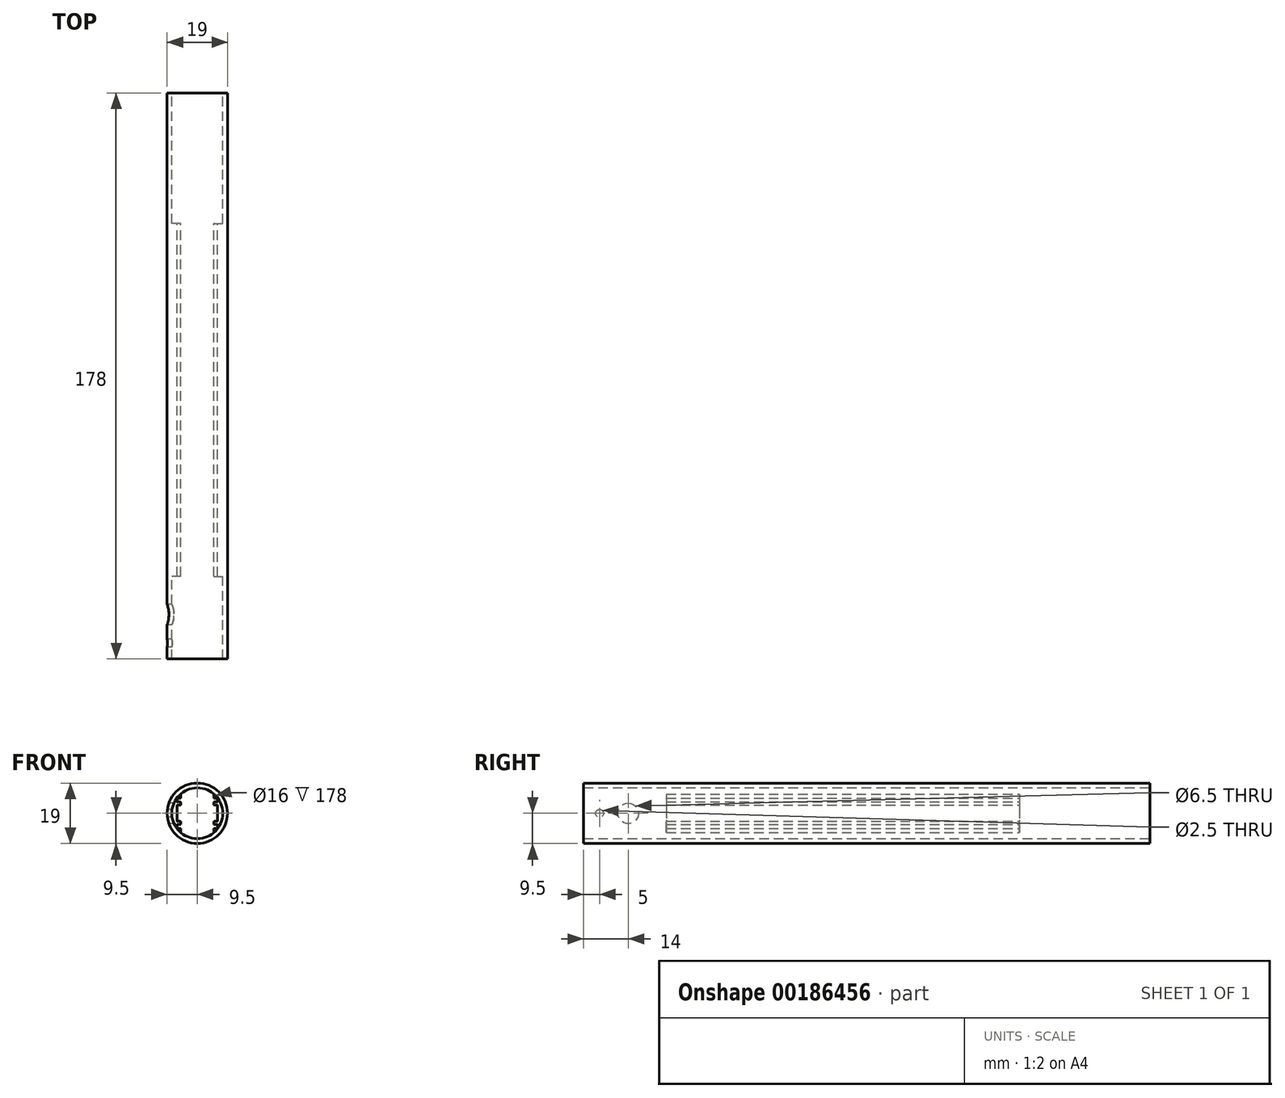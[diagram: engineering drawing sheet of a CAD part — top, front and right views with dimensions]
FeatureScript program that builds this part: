
annotation { "Feature Type Name" : "Feature", "Feature Type Description" : "" }
export const myFeature = defineFeature(function(context is Context, id is Id, definition is map)
    precondition{}
    {
        {
            assignVariable(context, id + "F0", {"name" : "Main_Diam", "anyValue" : 19});
        }
        {
            assignVariable(context, id + "F1", {"name" : "Main_Length", "anyValue" : 178});
        }
        {
            assignVariable(context, id + "F2", {"name" : "Bore_Depth_F", "anyValue" : 26});
        }
        {
            assignVariable(context, id + "F3", {"name" : "Bore_Depth_R", "anyValue" : 41});
        }
        {
            var Q0;
            Q0=qCreatedBy(makeId("Front.planeOp"),FACE);
            var sketch = newSketch(context, id + "F4", { "sketchPlane" : qUnion([Q0])});
            skLineSegment(sketch, "E0", {"start": v(-5.25, -3.45) * mm, "end": v(-5.25, -2.65) * mm});
            skLineSegment(sketch, "E1", {"start": v(9.2, 1.38) * mm, "end": v(9.42, 1.2) * mm});
            skArc(sketch, "E2", {"start": v(-5.35, -2.55) * mm, "mid": v(-5.28, -2.58) * mm, "end": v(-5.25, -2.65) * mm});
            skArc(sketch, "E3", {"start": v(6.3, 4.75) * mm, "mid": v(6.37, 4.72) * mm, "end": v(6.4, 4.65) * mm});
            skArc(sketch, "E4", {"start": v(-5.25, -6.04) * mm, "mid": v(0, -8) * mm, "end": v(5.25, -6.04) * mm});
            skLineSegment(sketch, "E5", {"start": v(1.53, 9.17) * mm, "end": v(1.78, 9.33) * mm});
            skLineSegment(sketch, "E6", {"start": v(-7.18, -5.91) * mm, "end": v(-7.2, -6.2) * mm});
            skArc(sketch, "E7", {"start": v(-8.33, -4.58) * mm, "mid": v(-8.23, -4.75) * mm, "end": v(-8.13, -4.92) * mm});
            skLineSegment(sketch, "E8", {"start": v(5.13, 7.76) * mm, "end": v(5.42, 7.8) * mm});
            skLineSegment(sketch, "E9", {"start": v(6.4, -2.45) * mm, "end": v(6.4, 0) * mm});
            skLineSegment(sketch, "E10", {"start": v(-2.33, -9) * mm, "end": v(-2.17, -9.25) * mm});
            skArc(sketch, "E11", {"start": v(8.97, -3.13) * mm, "mid": v(9.04, -2.94) * mm, "end": v(9.1, -2.74) * mm});
            skArc(sketch, "E12", {"start": v(-4.05, -8.6) * mm, "mid": v(-3.86, -8.68) * mm, "end": v(-3.68, -8.76) * mm});
            skArc(sketch, "E13", {"start": v(4.05, 8.6) * mm, "mid": v(3.86, 8.68) * mm, "end": v(3.68, 8.76) * mm});
            skLineSegment(sketch, "E14", {"start": v(6.63, 6.52) * mm, "end": v(6.92, 6.5) * mm});
            skArc(sketch, "E15", {"start": v(-6.4, 3.65) * mm, "mid": v(-6.37, 3.58) * mm, "end": v(-6.3, 3.55) * mm});
            skArc(sketch, "E16", {"start": v(5.74, 7.57) * mm, "mid": v(5.58, 7.69) * mm, "end": v(5.42, 7.8) * mm});
            skLineSegment(sketch, "E17", {"start": v(-9.2, 1.38) * mm, "end": v(-9.42, 1.2) * mm});
            skArc(sketch, "E18", {"start": v(1.78, -9.33) * mm, "mid": v(1.98, -9.3) * mm, "end": v(2.17, -9.25) * mm});
            skLineSegment(sketch, "E19", {"start": v(-5.8, 7.28) * mm, "end": v(-5.74, 7.57) * mm});
            skArc(sketch, "E20", {"start": v(-2.17, -9.25) * mm, "mid": v(-1.98, -9.3) * mm, "end": v(-1.78, -9.33) * mm});
            skLineSegment(sketch, "E21", {"start": v(7.84, 5) * mm, "end": v(8.13, 4.92) * mm});
            skLineSegment(sketch, "E22", {"start": v(2.33, 9) * mm, "end": v(2.17, 9.25) * mm});
            skArc(sketch, "E23", {"start": v(5.25, -3.45) * mm, "mid": v(5.28, -3.52) * mm, "end": v(5.35, -3.55) * mm});
            skLineSegment(sketch, "E24", {"start": v(5.8, -7.28) * mm, "end": v(5.74, -7.57) * mm});
            skArc(sketch, "E25", {"start": v(5.35, 2.55) * mm, "mid": v(5.28, 2.58) * mm, "end": v(5.25, 2.65) * mm});
            skArc(sketch, "E26", {"start": v(4.15, -8.32) * mm, "mid": v(4.65, -8.05) * mm, "end": v(5.13, -7.76) * mm});
            skArc(sketch, "E27", {"start": v(-5.35, 4.75) * mm, "mid": v(-5.28, 4.78) * mm, "end": v(-5.25, 4.85) * mm});
            skArc(sketch, "E28", {"start": v(-8.13, 4.92) * mm, "mid": v(-8.23, 4.75) * mm, "end": v(-8.33, 4.58) * mm});
            skLineSegment(sketch, "E29", {"start": v(7.84, -5) * mm, "end": v(8.13, -4.92) * mm});
            skArc(sketch, "E30", {"start": v(8.33, 4.58) * mm, "mid": v(8.23, 4.75) * mm, "end": v(8.13, 4.92) * mm});
            skLineSegment(sketch, "E31", {"start": v(-6.3, 3.55) * mm, "end": v(-5.35, 3.55) * mm});
            skLineSegment(sketch, "E32", {"start": v(-5.25, 3.45) * mm, "end": v(-5.25, 2.65) * mm});
            skArc(sketch, "E33", {"start": v(9.1, 2.74) * mm, "mid": v(9.04, 2.94) * mm, "end": v(8.97, 3.13) * mm});
            skLineSegment(sketch, "E34", {"start": v(6.3, 3.55) * mm, "end": v(5.35, 3.55) * mm});
            skLineSegment(sketch, "E35", {"start": v(4.15, -8.32) * mm, "end": v(4.05, -8.6) * mm});
            skLineSegment(sketch, "E36", {"start": v(5.25, 6.04) * mm, "end": v(5.25, 4.85) * mm});
            skArc(sketch, "E37", {"start": v(8.71, 3.26) * mm, "mid": v(8.5, 3.78) * mm, "end": v(8.25, 4.3) * mm});
            skArc(sketch, "E38", {"start": v(0.4, -9.3) * mm, "mid": v(0.97, -9.25) * mm, "end": v(1.53, -9.17) * mm});
            skArc(sketch, "E39", {"start": v(9.47, 0.8) * mm, "mid": v(9.45, 1) * mm, "end": v(9.42, 1.2) * mm});
            skArc(sketch, "E40", {"start": v(-4.15, 8.32) * mm, "mid": v(-4.65, 8.05) * mm, "end": v(-5.13, 7.76) * mm});
            skLineSegment(sketch, "E41", {"start": v(-0.4, 9.3) * mm, "end": v(-0.2, 9.5) * mm});
            skLineSegment(sketch, "E42", {"start": v(8.25, 4.3) * mm, "end": v(8.33, 4.58) * mm});
            skLineSegment(sketch, "E43", {"start": v(2.33, -9) * mm, "end": v(2.17, -9.25) * mm});
            skArc(sketch, "E44", {"start": v(-0.4, 9.3) * mm, "mid": v(-0.97, 9.25) * mm, "end": v(-1.53, 9.17) * mm});
            skLineSegment(sketch, "E45", {"start": v(-5.13, 7.76) * mm, "end": v(-5.42, 7.8) * mm});
            skLineSegment(sketch, "E46", {"start": v(-2.33, 9) * mm, "end": v(-2.17, 9.25) * mm});
            skLineSegment(sketch, "E47", {"start": v(6.63, -6.52) * mm, "end": v(6.92, -6.5) * mm});
            skArc(sketch, "E48", {"start": v(9.42, -1.2) * mm, "mid": v(9.45, -1) * mm, "end": v(9.47, -0.8) * mm});
            skArc(sketch, "E49", {"start": v(-3.68, 8.76) * mm, "mid": v(-3.86, 8.68) * mm, "end": v(-4.05, 8.6) * mm});
            skArc(sketch, "E50", {"start": v(9.2, 1.38) * mm, "mid": v(9.1, 1.93) * mm, "end": v(8.96, 2.48) * mm});
            skArc(sketch, "E51", {"start": v(5.35, 4.75) * mm, "mid": v(5.28, 4.78) * mm, "end": v(5.25, 4.85) * mm});
            skLineSegment(sketch, "E52", {"start": v(5.25, 3.45) * mm, "end": v(5.25, 2.65) * mm});
            skArc(sketch, "E53", {"start": v(-0.2, -9.5) * mm, "mid": v(0, -9.5) * mm, "end": v(0.2, -9.5) * mm});
            skArc(sketch, "E54", {"start": v(7.2, 6.2) * mm, "mid": v(7.06, 6.36) * mm, "end": v(6.92, 6.5) * mm});
            skLineSegment(sketch, "E55", {"start": v(3.4, 8.65) * mm, "end": v(3.68, 8.76) * mm});
            skArc(sketch, "E56", {"start": v(6.4, 3.65) * mm, "mid": v(6.37, 3.58) * mm, "end": v(6.3, 3.55) * mm});
            skLineSegment(sketch, "E57", {"start": v(-6.4, -2.45) * mm, "end": v(-6.4, 0) * mm});
            skArc(sketch, "E58", {"start": v(-2.33, 9) * mm, "mid": v(-2.87, 8.84) * mm, "end": v(-3.4, 8.65) * mm});
            skLineSegment(sketch, "E59", {"start": v(-1.53, 9.17) * mm, "end": v(-1.78, 9.33) * mm});
            skLineSegment(sketch, "E60", {"start": v(0.4, -9.3) * mm, "end": v(0.2, -9.5) * mm});
            skArc(sketch, "E61", {"start": v(-6.92, 6.5) * mm, "mid": v(-7.06, 6.36) * mm, "end": v(-7.2, 6.2) * mm});
            skArc(sketch, "E62", {"start": v(-8.25, 4.3) * mm, "mid": v(-8.5, 3.78) * mm, "end": v(-8.71, 3.26) * mm});
            skArc(sketch, "E63", {"start": v(6.3, -4.75) * mm, "mid": v(6.37, -4.72) * mm, "end": v(6.4, -4.65) * mm});
            skLineSegment(sketch, "E64", {"start": v(-6.4, 4.65) * mm, "end": v(-6.4, 3.65) * mm});
            skLineSegment(sketch, "E65", {"start": v(-6.4, 2.45) * mm, "end": v(-6.4, 0) * mm});
            skArc(sketch, "E66", {"start": v(8.25, -4.3) * mm, "mid": v(8.5, -3.78) * mm, "end": v(8.71, -3.26) * mm});
            skArc(sketch, "E67", {"start": v(-6.3, 2.55) * mm, "mid": v(-6.37, 2.52) * mm, "end": v(-6.4, 2.45) * mm});
            skLineSegment(sketch, "E68", {"start": v(-5.25, 6.04) * mm, "end": v(-5.25, 4.85) * mm});
            skLineSegment(sketch, "E69", {"start": v(-5.35, 4.75) * mm, "end": v(-6.3, 4.75) * mm});
            skLineSegment(sketch, "E70", {"start": v(-5.35, 2.55) * mm, "end": v(-6.3, 2.55) * mm});
            skArc(sketch, "E71", {"start": v(-5.25, 3.45) * mm, "mid": v(-5.28, 3.52) * mm, "end": v(-5.35, 3.55) * mm});
            skArc(sketch, "E72", {"start": v(-5.35, 2.55) * mm, "mid": v(-5.28, 2.58) * mm, "end": v(-5.25, 2.65) * mm});
            skArc(sketch, "E73", {"start": v(-6.3, 4.75) * mm, "mid": v(-6.37, 4.72) * mm, "end": v(-6.4, 4.65) * mm});
            skArc(sketch, "E74", {"start": v(6.3, 2.55) * mm, "mid": v(6.37, 2.52) * mm, "end": v(6.4, 2.45) * mm});
            skLineSegment(sketch, "E75", {"start": v(5.35, 2.55) * mm, "end": v(6.3, 2.55) * mm});
            skArc(sketch, "E76", {"start": v(5.25, 3.45) * mm, "mid": v(5.28, 3.52) * mm, "end": v(5.35, 3.55) * mm});
            skArc(sketch, "E77", {"start": v(0.2, 9.5) * mm, "mid": v(0, 9.5) * mm, "end": v(-0.2, 9.5) * mm});
            skLineSegment(sketch, "E78", {"start": v(5.35, 4.75) * mm, "end": v(6.3, 4.75) * mm});
            skLineSegment(sketch, "E79", {"start": v(6.4, 2.45) * mm, "end": v(6.4, 0) * mm});
            skLineSegment(sketch, "E80", {"start": v(6.4, 4.65) * mm, "end": v(6.4, 3.65) * mm});
            skArc(sketch, "E81", {"start": v(-5.35, -4.75) * mm, "mid": v(-5.28, -4.78) * mm, "end": v(-5.25, -4.85) * mm});
            skLineSegment(sketch, "E82", {"start": v(-6.3, -3.55) * mm, "end": v(-5.35, -3.55) * mm});
            skLineSegment(sketch, "E83", {"start": v(-5.35, -2.55) * mm, "end": v(-6.3, -2.55) * mm});
            skArc(sketch, "E84", {"start": v(-5.25, -3.45) * mm, "mid": v(-5.28, -3.52) * mm, "end": v(-5.35, -3.55) * mm});
            skArc(sketch, "E85", {"start": v(-6.3, -2.55) * mm, "mid": v(-6.37, -2.52) * mm, "end": v(-6.4, -2.45) * mm});
            skArc(sketch, "E86", {"start": v(-6.4, -3.65) * mm, "mid": v(-6.37, -3.58) * mm, "end": v(-6.3, -3.55) * mm});
            skArc(sketch, "E87", {"start": v(-6.3, -4.75) * mm, "mid": v(-6.37, -4.72) * mm, "end": v(-6.4, -4.65) * mm});
            skArc(sketch, "E88", {"start": v(5.35, -2.55) * mm, "mid": v(5.28, -2.58) * mm, "end": v(5.25, -2.65) * mm});
            skLineSegment(sketch, "E89", {"start": v(-3.4, 8.65) * mm, "end": v(-3.68, 8.76) * mm});
            skArc(sketch, "E90", {"start": v(6.3, -2.55) * mm, "mid": v(6.37, -2.52) * mm, "end": v(6.4, -2.45) * mm});
            skLineSegment(sketch, "E91", {"start": v(5.35, -2.55) * mm, "end": v(6.3, -2.55) * mm});
            skArc(sketch, "E92", {"start": v(6.4, -3.65) * mm, "mid": v(6.37, -3.58) * mm, "end": v(6.3, -3.55) * mm});
            skLineSegment(sketch, "E93", {"start": v(6.3, -3.55) * mm, "end": v(5.35, -3.55) * mm});
            skArc(sketch, "E94", {"start": v(5.35, -4.75) * mm, "mid": v(5.28, -4.78) * mm, "end": v(5.25, -4.85) * mm});
            skLineSegment(sketch, "E95", {"start": v(-5.25, -6.04) * mm, "end": v(-5.25, -4.85) * mm});
            skLineSegment(sketch, "E96", {"start": v(5.25, -3.45) * mm, "end": v(5.25, -2.65) * mm});
            skLineSegment(sketch, "E97", {"start": v(6.4, -4.65) * mm, "end": v(6.4, -3.65) * mm});
            skLineSegment(sketch, "E98", {"start": v(-5.35, -4.75) * mm, "end": v(-6.3, -4.75) * mm});
            skArc(sketch, "E99", {"start": v(-8.97, 3.13) * mm, "mid": v(-9.04, 2.94) * mm, "end": v(-9.1, 2.74) * mm});
            skLineSegment(sketch, "E100", {"start": v(-6.4, -4.65) * mm, "end": v(-6.4, -3.65) * mm});
            skLineSegment(sketch, "E101", {"start": v(5.35, -4.75) * mm, "end": v(6.3, -4.75) * mm});
            skLineSegment(sketch, "E102", {"start": v(-7.84, 5) * mm, "end": v(-8.13, 4.92) * mm});
            skLineSegment(sketch, "E103", {"start": v(5.25, -6.04) * mm, "end": v(5.25, -4.85) * mm});
            skArc(sketch, "E104", {"start": v(5.25, 6.04) * mm, "mid": v(0, 8) * mm, "end": v(-5.25, 6.04) * mm});
            skLineSegment(sketch, "E105", {"start": v(-0.4, -9.3) * mm, "end": v(-0.2, -9.5) * mm});
            skArc(sketch, "E106", {"start": v(2.33, -9) * mm, "mid": v(2.87, -8.84) * mm, "end": v(3.4, -8.65) * mm});
            skLineSegment(sketch, "E107", {"start": v(1.53, -9.17) * mm, "end": v(1.78, -9.33) * mm});
            skArc(sketch, "E108", {"start": v(3.68, -8.76) * mm, "mid": v(3.86, -8.68) * mm, "end": v(4.05, -8.6) * mm});
            skArc(sketch, "E109", {"start": v(-9.1, -2.74) * mm, "mid": v(-9.04, -2.94) * mm, "end": v(-8.97, -3.13) * mm});
            skLineSegment(sketch, "E110", {"start": v(3.4, -8.65) * mm, "end": v(3.68, -8.76) * mm});
            skArc(sketch, "E111", {"start": v(5.8, -7.28) * mm, "mid": v(6.22, -6.91) * mm, "end": v(6.63, -6.52) * mm});
            skArc(sketch, "E112", {"start": v(5.42, -7.8) * mm, "mid": v(5.58, -7.69) * mm, "end": v(5.74, -7.57) * mm});
            skLineSegment(sketch, "E113", {"start": v(5.13, -7.76) * mm, "end": v(5.42, -7.8) * mm});
            skLineSegment(sketch, "E114", {"start": v(-5.13, -7.76) * mm, "end": v(-5.42, -7.8) * mm});
            skLineSegment(sketch, "E115", {"start": v(7.18, -5.91) * mm, "end": v(7.2, -6.2) * mm});
            skLineSegment(sketch, "E116", {"start": v(-6.63, -6.52) * mm, "end": v(-6.92, -6.5) * mm});
            skArc(sketch, "E117", {"start": v(8.13, -4.92) * mm, "mid": v(8.23, -4.75) * mm, "end": v(8.33, -4.58) * mm});
            skArc(sketch, "E118", {"start": v(6.92, -6.5) * mm, "mid": v(7.06, -6.36) * mm, "end": v(7.2, -6.2) * mm});
            skArc(sketch, "E119", {"start": v(-5.74, -7.57) * mm, "mid": v(-5.58, -7.69) * mm, "end": v(-5.42, -7.8) * mm});
            skArc(sketch, "E120", {"start": v(8.96, -2.48) * mm, "mid": v(9.1, -1.93) * mm, "end": v(9.2, -1.38) * mm});
            skLineSegment(sketch, "E121", {"start": v(8.96, -2.48) * mm, "end": v(9.1, -2.74) * mm});
            skLineSegment(sketch, "E122", {"start": v(8.71, -3.26) * mm, "end": v(8.97, -3.13) * mm});
            skArc(sketch, "E123", {"start": v(9.28, -0.57) * mm, "mid": v(9.3, 0) * mm, "end": v(9.28, 0.57) * mm});
            skLineSegment(sketch, "E124", {"start": v(9.28, -0.57) * mm, "end": v(9.47, -0.8) * mm});
            skLineSegment(sketch, "E125", {"start": v(-1.53, -9.17) * mm, "end": v(-1.78, -9.33) * mm});
            skLineSegment(sketch, "E126", {"start": v(9.2, -1.38) * mm, "end": v(9.42, -1.2) * mm});
            skLineSegment(sketch, "E127", {"start": v(8.71, 3.26) * mm, "end": v(8.97, 3.13) * mm});
            skLineSegment(sketch, "E128", {"start": v(8.96, 2.48) * mm, "end": v(9.1, 2.74) * mm});
            skArc(sketch, "E129", {"start": v(7.84, 5) * mm, "mid": v(7.52, 5.47) * mm, "end": v(7.18, 5.91) * mm});
            skArc(sketch, "E130", {"start": v(6.63, 6.52) * mm, "mid": v(6.22, 6.91) * mm, "end": v(5.8, 7.28) * mm});
            skLineSegment(sketch, "E131", {"start": v(7.18, 5.91) * mm, "end": v(7.2, 6.2) * mm});
            skArc(sketch, "E132", {"start": v(5.13, 7.76) * mm, "mid": v(4.65, 8.05) * mm, "end": v(4.15, 8.32) * mm});
            skLineSegment(sketch, "E133", {"start": v(5.8, 7.28) * mm, "end": v(5.74, 7.57) * mm});
            skArc(sketch, "E134", {"start": v(3.4, 8.65) * mm, "mid": v(2.87, 8.84) * mm, "end": v(2.33, 9) * mm});
            skLineSegment(sketch, "E135", {"start": v(4.15, 8.32) * mm, "end": v(4.05, 8.6) * mm});
            skArc(sketch, "E136", {"start": v(1.53, 9.17) * mm, "mid": v(0.97, 9.25) * mm, "end": v(0.4, 9.3) * mm});
            skArc(sketch, "E137", {"start": v(2.17, 9.25) * mm, "mid": v(1.98, 9.3) * mm, "end": v(1.78, 9.33) * mm});
            skLineSegment(sketch, "E138", {"start": v(0.4, 9.3) * mm, "end": v(0.2, 9.5) * mm});
            skArc(sketch, "E139", {"start": v(-1.78, 9.33) * mm, "mid": v(-1.98, 9.3) * mm, "end": v(-2.17, 9.25) * mm});
            skLineSegment(sketch, "E140", {"start": v(-4.15, 8.32) * mm, "end": v(-4.05, 8.6) * mm});
            skArc(sketch, "E141", {"start": v(-5.8, 7.28) * mm, "mid": v(-6.22, 6.91) * mm, "end": v(-6.63, 6.52) * mm});
            skArc(sketch, "E142", {"start": v(-5.42, 7.8) * mm, "mid": v(-5.58, 7.69) * mm, "end": v(-5.74, 7.57) * mm});
            skLineSegment(sketch, "E143", {"start": v(-9.2, -1.38) * mm, "end": v(-9.42, -1.2) * mm});
            skLineSegment(sketch, "E144", {"start": v(-7.18, 5.91) * mm, "end": v(-7.2, 6.2) * mm});
            skLineSegment(sketch, "E145", {"start": v(-6.63, 6.52) * mm, "end": v(-6.92, 6.5) * mm});
            skArc(sketch, "E146", {"start": v(-8.96, 2.48) * mm, "mid": v(-9.1, 1.93) * mm, "end": v(-9.2, 1.38) * mm});
            skLineSegment(sketch, "E147", {"start": v(-8.96, 2.48) * mm, "end": v(-9.1, 2.74) * mm});
            skLineSegment(sketch, "E148", {"start": v(-8.71, 3.26) * mm, "end": v(-8.97, 3.13) * mm});
            skArc(sketch, "E149", {"start": v(-9.28, 0.57) * mm, "mid": v(-9.3, 0) * mm, "end": v(-9.28, -0.57) * mm});
            skArc(sketch, "E150", {"start": v(-9.42, 1.2) * mm, "mid": v(-9.45, 1) * mm, "end": v(-9.47, 0.8) * mm});
            skLineSegment(sketch, "E151", {"start": v(-9.28, 0.57) * mm, "end": v(-9.47, 0.8) * mm});
            skLineSegment(sketch, "E152", {"start": v(8.25, -4.3) * mm, "end": v(8.33, -4.58) * mm});
            skArc(sketch, "E153", {"start": v(-9.2, -1.38) * mm, "mid": v(-9.1, -1.93) * mm, "end": v(-8.96, -2.48) * mm});
            skArc(sketch, "E154", {"start": v(-9.47, -0.8) * mm, "mid": v(-9.45, -1) * mm, "end": v(-9.42, -1.2) * mm});
            skLineSegment(sketch, "E155", {"start": v(-9.28, -0.57) * mm, "end": v(-9.47, -0.8) * mm});
            skArc(sketch, "E156", {"start": v(-8.71, -3.26) * mm, "mid": v(-8.5, -3.78) * mm, "end": v(-8.25, -4.3) * mm});
            skLineSegment(sketch, "E157", {"start": v(-8.71, -3.26) * mm, "end": v(-8.97, -3.13) * mm});
            skLineSegment(sketch, "E158", {"start": v(-8.96, -2.48) * mm, "end": v(-9.1, -2.74) * mm});
            skArc(sketch, "E159", {"start": v(-7.84, -5) * mm, "mid": v(-7.52, -5.47) * mm, "end": v(-7.18, -5.91) * mm});
            skLineSegment(sketch, "E160", {"start": v(-7.84, -5) * mm, "end": v(-8.13, -4.92) * mm});
            skLineSegment(sketch, "E161", {"start": v(-8.25, -4.3) * mm, "end": v(-8.33, -4.58) * mm});
            skArc(sketch, "E162", {"start": v(-6.63, -6.52) * mm, "mid": v(-6.22, -6.91) * mm, "end": v(-5.8, -7.28) * mm});
            skLineSegment(sketch, "E163", {"start": v(9.28, 0.57) * mm, "end": v(9.47, 0.8) * mm});
            skArc(sketch, "E164", {"start": v(-7.2, -6.2) * mm, "mid": v(-7.06, -6.36) * mm, "end": v(-6.92, -6.5) * mm});
            skArc(sketch, "E165", {"start": v(7.18, -5.91) * mm, "mid": v(7.52, -5.47) * mm, "end": v(7.84, -5) * mm});
            skLineSegment(sketch, "E166", {"start": v(-5.8, -7.28) * mm, "end": v(-5.74, -7.57) * mm});
            skArc(sketch, "E167", {"start": v(-3.4, -8.65) * mm, "mid": v(-2.87, -8.84) * mm, "end": v(-2.33, -9) * mm});
            skLineSegment(sketch, "E168", {"start": v(-3.4, -8.65) * mm, "end": v(-3.68, -8.76) * mm});
            skLineSegment(sketch, "E169", {"start": v(-4.15, -8.32) * mm, "end": v(-4.05, -8.6) * mm});
            skArc(sketch, "E170", {"start": v(-1.53, -9.17) * mm, "mid": v(-0.97, -9.25) * mm, "end": v(-0.4, -9.3) * mm});
            skArc(sketch, "E171", {"start": v(-7.18, 5.91) * mm, "mid": v(-7.52, 5.47) * mm, "end": v(-7.84, 5) * mm});
            skLineSegment(sketch, "E172", {"start": v(-8.25, 4.3) * mm, "end": v(-8.33, 4.58) * mm});
            skArc(sketch, "E173", {"start": v(-5.13, -7.76) * mm, "mid": v(-4.65, -8.05) * mm, "end": v(-4.15, -8.32) * mm});
            skSolve(sketch);
        }
        {
            var Q0;
            Q0=makeQuery(id+"F4.imprint","IMPRINT",FACE,{"disambiguationData":[TD([[makeQuery(id+"F4.imprint","IMPRINT",EDGE,{"derivedFrom":sQuery(id+"F4.wireOp",EDGE,"E0")}),1.0]])]});
            extrude(context, id + "F5", {"entities" : qUnion([Q0]), "depth" : (getVariable(context, 'Main_Length') - getVariable(context, 'Bore_Depth_F') - getVariable(context, 'Bore_Depth_R')) * mm});
        }
        {
            var Q0;
            Q0=makeQuery(id+"F5.opExtrude","CAP_FACE",FACE,{"disambiguationData":[OSD([sQuery(id+"F4.wireOp",EDGE,"E0"),sQuery(id+"F4.wireOp",EDGE,"E1"),sQuery(id+"F4.wireOp",EDGE,"E2"),sQuery(id+"F4.wireOp",EDGE,"E3"),sQuery(id+"F4.wireOp",EDGE,"E4"),sQuery(id+"F4.wireOp",EDGE,"E5"),sQuery(id+"F4.wireOp",EDGE,"E6"),sQuery(id+"F4.wireOp",EDGE,"E7"),sQuery(id+"F4.wireOp",EDGE,"E8"),sQuery(id+"F4.wireOp",EDGE,"E9"),sQuery(id+"F4.wireOp",EDGE,"E10"),sQuery(id+"F4.wireOp",EDGE,"E11"),sQuery(id+"F4.wireOp",EDGE,"E12"),sQuery(id+"F4.wireOp",EDGE,"E13"),sQuery(id+"F4.wireOp",EDGE,"E14"),sQuery(id+"F4.wireOp",EDGE,"E15"),sQuery(id+"F4.wireOp",EDGE,"E16"),sQuery(id+"F4.wireOp",EDGE,"E17"),sQuery(id+"F4.wireOp",EDGE,"E18"),sQuery(id+"F4.wireOp",EDGE,"E19"),sQuery(id+"F4.wireOp",EDGE,"E20"),sQuery(id+"F4.wireOp",EDGE,"E21"),sQuery(id+"F4.wireOp",EDGE,"E22"),sQuery(id+"F4.wireOp",EDGE,"E23"),sQuery(id+"F4.wireOp",EDGE,"E24"),sQuery(id+"F4.wireOp",EDGE,"E25"),sQuery(id+"F4.wireOp",EDGE,"E26"),sQuery(id+"F4.wireOp",EDGE,"E27"),sQuery(id+"F4.wireOp",EDGE,"E28"),sQuery(id+"F4.wireOp",EDGE,"E29"),sQuery(id+"F4.wireOp",EDGE,"E30"),sQuery(id+"F4.wireOp",EDGE,"E31"),sQuery(id+"F4.wireOp",EDGE,"E32"),sQuery(id+"F4.wireOp",EDGE,"E33"),sQuery(id+"F4.wireOp",EDGE,"E34"),sQuery(id+"F4.wireOp",EDGE,"E35"),sQuery(id+"F4.wireOp",EDGE,"E36"),sQuery(id+"F4.wireOp",EDGE,"E37"),sQuery(id+"F4.wireOp",EDGE,"E38"),sQuery(id+"F4.wireOp",EDGE,"E39"),sQuery(id+"F4.wireOp",EDGE,"E40"),sQuery(id+"F4.wireOp",EDGE,"E41"),sQuery(id+"F4.wireOp",EDGE,"E42"),sQuery(id+"F4.wireOp",EDGE,"E43"),sQuery(id+"F4.wireOp",EDGE,"E44"),sQuery(id+"F4.wireOp",EDGE,"E45"),sQuery(id+"F4.wireOp",EDGE,"E46"),sQuery(id+"F4.wireOp",EDGE,"E47"),sQuery(id+"F4.wireOp",EDGE,"E48"),sQuery(id+"F4.wireOp",EDGE,"E49"),sQuery(id+"F4.wireOp",EDGE,"E50"),sQuery(id+"F4.wireOp",EDGE,"E51"),sQuery(id+"F4.wireOp",EDGE,"E52"),sQuery(id+"F4.wireOp",EDGE,"E53"),sQuery(id+"F4.wireOp",EDGE,"E54"),sQuery(id+"F4.wireOp",EDGE,"E55"),sQuery(id+"F4.wireOp",EDGE,"E56"),sQuery(id+"F4.wireOp",EDGE,"E57"),sQuery(id+"F4.wireOp",EDGE,"E58"),sQuery(id+"F4.wireOp",EDGE,"E59"),sQuery(id+"F4.wireOp",EDGE,"E60"),sQuery(id+"F4.wireOp",EDGE,"E61"),sQuery(id+"F4.wireOp",EDGE,"E62"),sQuery(id+"F4.wireOp",EDGE,"E63"),sQuery(id+"F4.wireOp",EDGE,"E64"),sQuery(id+"F4.wireOp",EDGE,"E65"),sQuery(id+"F4.wireOp",EDGE,"E66"),sQuery(id+"F4.wireOp",EDGE,"E67"),sQuery(id+"F4.wireOp",EDGE,"E68"),sQuery(id+"F4.wireOp",EDGE,"E69"),sQuery(id+"F4.wireOp",EDGE,"E70"),sQuery(id+"F4.wireOp",EDGE,"E71"),sQuery(id+"F4.wireOp",EDGE,"E72"),sQuery(id+"F4.wireOp",EDGE,"E73"),sQuery(id+"F4.wireOp",EDGE,"E74"),sQuery(id+"F4.wireOp",EDGE,"E75"),sQuery(id+"F4.wireOp",EDGE,"E76"),sQuery(id+"F4.wireOp",EDGE,"E77"),sQuery(id+"F4.wireOp",EDGE,"E78"),sQuery(id+"F4.wireOp",EDGE,"E79"),sQuery(id+"F4.wireOp",EDGE,"E80"),sQuery(id+"F4.wireOp",EDGE,"E81"),sQuery(id+"F4.wireOp",EDGE,"E82"),sQuery(id+"F4.wireOp",EDGE,"E83"),sQuery(id+"F4.wireOp",EDGE,"E84"),sQuery(id+"F4.wireOp",EDGE,"E85"),sQuery(id+"F4.wireOp",EDGE,"E86"),sQuery(id+"F4.wireOp",EDGE,"E87"),sQuery(id+"F4.wireOp",EDGE,"E88"),sQuery(id+"F4.wireOp",EDGE,"E89"),sQuery(id+"F4.wireOp",EDGE,"E90"),sQuery(id+"F4.wireOp",EDGE,"E91"),sQuery(id+"F4.wireOp",EDGE,"E92"),sQuery(id+"F4.wireOp",EDGE,"E93"),sQuery(id+"F4.wireOp",EDGE,"E94"),sQuery(id+"F4.wireOp",EDGE,"E95"),sQuery(id+"F4.wireOp",EDGE,"E96"),sQuery(id+"F4.wireOp",EDGE,"E97"),sQuery(id+"F4.wireOp",EDGE,"E98"),sQuery(id+"F4.wireOp",EDGE,"E99"),sQuery(id+"F4.wireOp",EDGE,"E100"),sQuery(id+"F4.wireOp",EDGE,"E101"),sQuery(id+"F4.wireOp",EDGE,"E102"),sQuery(id+"F4.wireOp",EDGE,"E103"),sQuery(id+"F4.wireOp",EDGE,"E104"),sQuery(id+"F4.wireOp",EDGE,"E105"),sQuery(id+"F4.wireOp",EDGE,"E106"),sQuery(id+"F4.wireOp",EDGE,"E107"),sQuery(id+"F4.wireOp",EDGE,"E108"),sQuery(id+"F4.wireOp",EDGE,"E109"),sQuery(id+"F4.wireOp",EDGE,"E110"),sQuery(id+"F4.wireOp",EDGE,"E111"),sQuery(id+"F4.wireOp",EDGE,"E112"),sQuery(id+"F4.wireOp",EDGE,"E113"),sQuery(id+"F4.wireOp",EDGE,"E114"),sQuery(id+"F4.wireOp",EDGE,"E115"),sQuery(id+"F4.wireOp",EDGE,"E116"),sQuery(id+"F4.wireOp",EDGE,"E117"),sQuery(id+"F4.wireOp",EDGE,"E118"),sQuery(id+"F4.wireOp",EDGE,"E119"),sQuery(id+"F4.wireOp",EDGE,"E120"),sQuery(id+"F4.wireOp",EDGE,"E121"),sQuery(id+"F4.wireOp",EDGE,"E122"),sQuery(id+"F4.wireOp",EDGE,"E123"),sQuery(id+"F4.wireOp",EDGE,"E124"),sQuery(id+"F4.wireOp",EDGE,"E125"),sQuery(id+"F4.wireOp",EDGE,"E126"),sQuery(id+"F4.wireOp",EDGE,"E127"),sQuery(id+"F4.wireOp",EDGE,"E128"),sQuery(id+"F4.wireOp",EDGE,"E129"),sQuery(id+"F4.wireOp",EDGE,"E130"),sQuery(id+"F4.wireOp",EDGE,"E131"),sQuery(id+"F4.wireOp",EDGE,"E132"),sQuery(id+"F4.wireOp",EDGE,"E133"),sQuery(id+"F4.wireOp",EDGE,"E134"),sQuery(id+"F4.wireOp",EDGE,"E135"),sQuery(id+"F4.wireOp",EDGE,"E136"),sQuery(id+"F4.wireOp",EDGE,"E137"),sQuery(id+"F4.wireOp",EDGE,"E138"),sQuery(id+"F4.wireOp",EDGE,"E139"),sQuery(id+"F4.wireOp",EDGE,"E140"),sQuery(id+"F4.wireOp",EDGE,"E141"),sQuery(id+"F4.wireOp",EDGE,"E142"),sQuery(id+"F4.wireOp",EDGE,"E143"),sQuery(id+"F4.wireOp",EDGE,"E144"),sQuery(id+"F4.wireOp",EDGE,"E145"),sQuery(id+"F4.wireOp",EDGE,"E146"),sQuery(id+"F4.wireOp",EDGE,"E147"),sQuery(id+"F4.wireOp",EDGE,"E148"),sQuery(id+"F4.wireOp",EDGE,"E149"),sQuery(id+"F4.wireOp",EDGE,"E150"),sQuery(id+"F4.wireOp",EDGE,"E151"),sQuery(id+"F4.wireOp",EDGE,"E152"),sQuery(id+"F4.wireOp",EDGE,"E153"),sQuery(id+"F4.wireOp",EDGE,"E154"),sQuery(id+"F4.wireOp",EDGE,"E155"),sQuery(id+"F4.wireOp",EDGE,"E156"),sQuery(id+"F4.wireOp",EDGE,"E157"),sQuery(id+"F4.wireOp",EDGE,"E158"),sQuery(id+"F4.wireOp",EDGE,"E159"),sQuery(id+"F4.wireOp",EDGE,"E160"),sQuery(id+"F4.wireOp",EDGE,"E161"),sQuery(id+"F4.wireOp",EDGE,"E162"),sQuery(id+"F4.wireOp",EDGE,"E163"),sQuery(id+"F4.wireOp",EDGE,"E164"),sQuery(id+"F4.wireOp",EDGE,"E165"),sQuery(id+"F4.wireOp",EDGE,"E166"),sQuery(id+"F4.wireOp",EDGE,"E167"),sQuery(id+"F4.wireOp",EDGE,"E168"),sQuery(id+"F4.wireOp",EDGE,"E169"),sQuery(id+"F4.wireOp",EDGE,"E170"),sQuery(id+"F4.wireOp",EDGE,"E171"),sQuery(id+"F4.wireOp",EDGE,"E172"),sQuery(id+"F4.wireOp",EDGE,"E173")])],"isStart":false});
            var sketch = newSketch(context, id + "F6", { "sketchPlane" : qUnion([Q0])});
            skCircle(sketch, "E174", {"center": v(0, 0) * mm, "radius": 8 * mm});
            skLineSegment(sketch, "E175.0.0", {"start": v(9.42, 1.2) * mm, "end": v(9.2, 1.38) * mm});
            skArc(sketch, "E175.0.1", {"start": v(9.2, 1.38) * mm, "mid": v(9.1, 1.93) * mm, "end": v(8.96, 2.48) * mm});
            skLineSegment(sketch, "E175.0.2", {"start": v(8.96, 2.48) * mm, "end": v(9.1, 2.74) * mm});
            skArc(sketch, "E175.0.3", {"start": v(9.1, 2.74) * mm, "mid": v(9.04, 2.94) * mm, "end": v(8.97, 3.13) * mm});
            skLineSegment(sketch, "E175.0.4", {"start": v(8.97, 3.13) * mm, "end": v(8.71, 3.26) * mm});
            skArc(sketch, "E175.0.5", {"start": v(8.71, 3.26) * mm, "mid": v(8.5, 3.78) * mm, "end": v(8.25, 4.3) * mm});
            skLineSegment(sketch, "E175.0.6", {"start": v(8.25, 4.3) * mm, "end": v(8.33, 4.58) * mm});
            skArc(sketch, "E175.0.7", {"start": v(8.33, 4.58) * mm, "mid": v(8.23, 4.75) * mm, "end": v(8.13, 4.92) * mm});
            skLineSegment(sketch, "E175.0.8", {"start": v(8.13, 4.92) * mm, "end": v(7.84, 5) * mm});
            skArc(sketch, "E175.0.9", {"start": v(7.84, 5) * mm, "mid": v(7.52, 5.47) * mm, "end": v(7.18, 5.91) * mm});
            skLineSegment(sketch, "E175.0.10", {"start": v(7.18, 5.91) * mm, "end": v(7.2, 6.2) * mm});
            skArc(sketch, "E175.0.11", {"start": v(7.2, 6.2) * mm, "mid": v(7.06, 6.36) * mm, "end": v(6.92, 6.5) * mm});
            skLineSegment(sketch, "E175.0.12", {"start": v(6.92, 6.5) * mm, "end": v(6.63, 6.52) * mm});
            skArc(sketch, "E175.0.13", {"start": v(6.63, 6.52) * mm, "mid": v(6.22, 6.91) * mm, "end": v(5.8, 7.28) * mm});
            skLineSegment(sketch, "E175.0.14", {"start": v(5.8, 7.28) * mm, "end": v(5.74, 7.57) * mm});
            skArc(sketch, "E175.0.15", {"start": v(5.74, 7.57) * mm, "mid": v(5.58, 7.69) * mm, "end": v(5.42, 7.8) * mm});
            skLineSegment(sketch, "E175.0.16", {"start": v(5.42, 7.8) * mm, "end": v(5.13, 7.76) * mm});
            skArc(sketch, "E175.0.17", {"start": v(5.13, 7.76) * mm, "mid": v(4.65, 8.05) * mm, "end": v(4.15, 8.32) * mm});
            skLineSegment(sketch, "E175.0.18", {"start": v(4.15, 8.32) * mm, "end": v(4.05, 8.6) * mm});
            skArc(sketch, "E175.0.19", {"start": v(4.05, 8.6) * mm, "mid": v(3.86, 8.68) * mm, "end": v(3.68, 8.76) * mm});
            skLineSegment(sketch, "E175.0.20", {"start": v(3.68, 8.76) * mm, "end": v(3.4, 8.65) * mm});
            skArc(sketch, "E175.0.21", {"start": v(3.4, 8.65) * mm, "mid": v(2.87, 8.84) * mm, "end": v(2.33, 9) * mm});
            skLineSegment(sketch, "E175.0.22", {"start": v(2.33, 9) * mm, "end": v(2.17, 9.25) * mm});
            skArc(sketch, "E175.0.23", {"start": v(2.17, 9.25) * mm, "mid": v(1.98, 9.3) * mm, "end": v(1.78, 9.33) * mm});
            skLineSegment(sketch, "E175.0.24", {"start": v(1.78, 9.33) * mm, "end": v(1.53, 9.17) * mm});
            skArc(sketch, "E175.0.25", {"start": v(1.53, 9.17) * mm, "mid": v(0.97, 9.25) * mm, "end": v(0.4, 9.3) * mm});
            skLineSegment(sketch, "E175.0.26", {"start": v(0.4, 9.3) * mm, "end": v(0.2, 9.5) * mm});
            skArc(sketch, "E175.0.27", {"start": v(0.2, 9.5) * mm, "mid": v(0, 9.5) * mm, "end": v(-0.2, 9.5) * mm});
            skLineSegment(sketch, "E175.0.28", {"start": v(-0.2, 9.5) * mm, "end": v(-0.4, 9.3) * mm});
            skArc(sketch, "E175.0.29", {"start": v(-0.4, 9.3) * mm, "mid": v(-0.97, 9.25) * mm, "end": v(-1.53, 9.17) * mm});
            skLineSegment(sketch, "E175.0.30", {"start": v(-1.53, 9.17) * mm, "end": v(-1.78, 9.33) * mm});
            skArc(sketch, "E175.0.31", {"start": v(-1.78, 9.33) * mm, "mid": v(-1.98, 9.3) * mm, "end": v(-2.17, 9.25) * mm});
            skLineSegment(sketch, "E175.0.32", {"start": v(-2.17, 9.25) * mm, "end": v(-2.33, 9) * mm});
            skArc(sketch, "E175.0.33", {"start": v(-2.33, 9) * mm, "mid": v(-2.87, 8.84) * mm, "end": v(-3.4, 8.65) * mm});
            skLineSegment(sketch, "E175.0.34", {"start": v(-3.4, 8.65) * mm, "end": v(-3.68, 8.76) * mm});
            skArc(sketch, "E175.0.35", {"start": v(-3.68, 8.76) * mm, "mid": v(-3.86, 8.68) * mm, "end": v(-4.05, 8.6) * mm});
            skLineSegment(sketch, "E175.0.36", {"start": v(-4.05, 8.6) * mm, "end": v(-4.15, 8.32) * mm});
            skArc(sketch, "E175.0.37", {"start": v(-4.15, 8.32) * mm, "mid": v(-4.65, 8.05) * mm, "end": v(-5.13, 7.76) * mm});
            skLineSegment(sketch, "E175.0.38", {"start": v(-5.13, 7.76) * mm, "end": v(-5.42, 7.8) * mm});
            skArc(sketch, "E175.0.39", {"start": v(-5.42, 7.8) * mm, "mid": v(-5.58, 7.69) * mm, "end": v(-5.74, 7.57) * mm});
            skLineSegment(sketch, "E175.0.40", {"start": v(-5.74, 7.57) * mm, "end": v(-5.8, 7.28) * mm});
            skArc(sketch, "E175.0.41", {"start": v(-5.8, 7.28) * mm, "mid": v(-6.22, 6.91) * mm, "end": v(-6.63, 6.52) * mm});
            skLineSegment(sketch, "E175.0.42", {"start": v(-6.63, 6.52) * mm, "end": v(-6.92, 6.5) * mm});
            skArc(sketch, "E175.0.43", {"start": v(-6.92, 6.5) * mm, "mid": v(-7.06, 6.36) * mm, "end": v(-7.2, 6.2) * mm});
            skLineSegment(sketch, "E175.0.44", {"start": v(-7.2, 6.2) * mm, "end": v(-7.18, 5.91) * mm});
            skArc(sketch, "E175.0.45", {"start": v(-7.18, 5.91) * mm, "mid": v(-7.52, 5.47) * mm, "end": v(-7.84, 5) * mm});
            skLineSegment(sketch, "E175.0.46", {"start": v(-7.84, 5) * mm, "end": v(-8.13, 4.92) * mm});
            skArc(sketch, "E175.0.47", {"start": v(-8.13, 4.92) * mm, "mid": v(-8.23, 4.75) * mm, "end": v(-8.33, 4.58) * mm});
            skLineSegment(sketch, "E175.0.48", {"start": v(-8.33, 4.58) * mm, "end": v(-8.25, 4.3) * mm});
            skArc(sketch, "E175.0.49", {"start": v(-8.25, 4.3) * mm, "mid": v(-8.5, 3.78) * mm, "end": v(-8.71, 3.26) * mm});
            skLineSegment(sketch, "E175.0.50", {"start": v(-8.71, 3.26) * mm, "end": v(-8.97, 3.13) * mm});
            skArc(sketch, "E175.0.51", {"start": v(-8.97, 3.13) * mm, "mid": v(-9.04, 2.94) * mm, "end": v(-9.1, 2.74) * mm});
            skLineSegment(sketch, "E175.0.52", {"start": v(-9.1, 2.74) * mm, "end": v(-8.96, 2.48) * mm});
            skArc(sketch, "E175.0.53", {"start": v(-8.96, 2.48) * mm, "mid": v(-9.1, 1.93) * mm, "end": v(-9.2, 1.38) * mm});
            skLineSegment(sketch, "E175.0.54", {"start": v(-9.2, 1.38) * mm, "end": v(-9.42, 1.2) * mm});
            skArc(sketch, "E175.0.55", {"start": v(-9.42, 1.2) * mm, "mid": v(-9.45, 1) * mm, "end": v(-9.47, 0.8) * mm});
            skLineSegment(sketch, "E175.0.56", {"start": v(-9.47, 0.8) * mm, "end": v(-9.28, 0.57) * mm});
            skArc(sketch, "E175.0.57", {"start": v(-9.28, 0.57) * mm, "mid": v(-9.3, 0) * mm, "end": v(-9.28, -0.57) * mm});
            skLineSegment(sketch, "E175.0.58", {"start": v(-9.28, -0.57) * mm, "end": v(-9.47, -0.8) * mm});
            skArc(sketch, "E175.0.59", {"start": v(-9.47, -0.8) * mm, "mid": v(-9.45, -1) * mm, "end": v(-9.42, -1.2) * mm});
            skLineSegment(sketch, "E175.0.60", {"start": v(-9.42, -1.2) * mm, "end": v(-9.2, -1.38) * mm});
            skArc(sketch, "E175.0.61", {"start": v(-9.2, -1.38) * mm, "mid": v(-9.1, -1.93) * mm, "end": v(-8.96, -2.48) * mm});
            skLineSegment(sketch, "E175.0.62", {"start": v(-8.96, -2.48) * mm, "end": v(-9.1, -2.74) * mm});
            skArc(sketch, "E175.0.63", {"start": v(-9.1, -2.74) * mm, "mid": v(-9.04, -2.94) * mm, "end": v(-8.97, -3.13) * mm});
            skLineSegment(sketch, "E175.0.64", {"start": v(-8.97, -3.13) * mm, "end": v(-8.71, -3.26) * mm});
            skArc(sketch, "E175.0.65", {"start": v(-8.71, -3.26) * mm, "mid": v(-8.5, -3.78) * mm, "end": v(-8.25, -4.3) * mm});
            skLineSegment(sketch, "E175.0.66", {"start": v(-8.25, -4.3) * mm, "end": v(-8.33, -4.58) * mm});
            skArc(sketch, "E175.0.67", {"start": v(-8.33, -4.58) * mm, "mid": v(-8.23, -4.75) * mm, "end": v(-8.13, -4.92) * mm});
            skLineSegment(sketch, "E175.0.68", {"start": v(-8.13, -4.92) * mm, "end": v(-7.84, -5) * mm});
            skArc(sketch, "E175.0.69", {"start": v(-7.84, -5) * mm, "mid": v(-7.52, -5.47) * mm, "end": v(-7.18, -5.91) * mm});
            skLineSegment(sketch, "E175.0.70", {"start": v(-7.18, -5.91) * mm, "end": v(-7.2, -6.2) * mm});
            skArc(sketch, "E175.0.71", {"start": v(-7.2, -6.2) * mm, "mid": v(-7.06, -6.36) * mm, "end": v(-6.92, -6.5) * mm});
            skLineSegment(sketch, "E175.0.72", {"start": v(-6.92, -6.5) * mm, "end": v(-6.63, -6.52) * mm});
            skArc(sketch, "E175.0.73", {"start": v(-6.63, -6.52) * mm, "mid": v(-6.22, -6.91) * mm, "end": v(-5.8, -7.28) * mm});
            skLineSegment(sketch, "E175.0.74", {"start": v(-5.8, -7.28) * mm, "end": v(-5.74, -7.57) * mm});
            skArc(sketch, "E175.0.75", {"start": v(-5.74, -7.57) * mm, "mid": v(-5.58, -7.69) * mm, "end": v(-5.42, -7.8) * mm});
            skLineSegment(sketch, "E175.0.76", {"start": v(-5.42, -7.8) * mm, "end": v(-5.13, -7.76) * mm});
            skArc(sketch, "E175.0.77", {"start": v(-5.13, -7.76) * mm, "mid": v(-4.65, -8.05) * mm, "end": v(-4.15, -8.32) * mm});
            skLineSegment(sketch, "E175.0.78", {"start": v(-4.15, -8.32) * mm, "end": v(-4.05, -8.6) * mm});
            skArc(sketch, "E175.0.79", {"start": v(-4.05, -8.6) * mm, "mid": v(-3.86, -8.68) * mm, "end": v(-3.68, -8.76) * mm});
            skLineSegment(sketch, "E175.0.80", {"start": v(-3.68, -8.76) * mm, "end": v(-3.4, -8.65) * mm});
            skArc(sketch, "E175.0.81", {"start": v(-3.4, -8.65) * mm, "mid": v(-2.87, -8.84) * mm, "end": v(-2.33, -9) * mm});
            skLineSegment(sketch, "E175.0.82", {"start": v(-2.33, -9) * mm, "end": v(-2.17, -9.25) * mm});
            skArc(sketch, "E175.0.83", {"start": v(-2.17, -9.25) * mm, "mid": v(-1.98, -9.3) * mm, "end": v(-1.78, -9.33) * mm});
            skLineSegment(sketch, "E175.0.84", {"start": v(-1.78, -9.33) * mm, "end": v(-1.53, -9.17) * mm});
            skArc(sketch, "E175.0.85", {"start": v(-1.53, -9.17) * mm, "mid": v(-0.97, -9.25) * mm, "end": v(-0.4, -9.3) * mm});
            skLineSegment(sketch, "E175.0.86", {"start": v(-0.4, -9.3) * mm, "end": v(-0.2, -9.5) * mm});
            skArc(sketch, "E175.0.87", {"start": v(-0.2, -9.5) * mm, "mid": v(0, -9.5) * mm, "end": v(0.2, -9.5) * mm});
            skLineSegment(sketch, "E175.0.88", {"start": v(0.2, -9.5) * mm, "end": v(0.4, -9.3) * mm});
            skArc(sketch, "E175.0.89", {"start": v(0.4, -9.3) * mm, "mid": v(0.97, -9.25) * mm, "end": v(1.53, -9.17) * mm});
            skLineSegment(sketch, "E175.0.90", {"start": v(1.53, -9.17) * mm, "end": v(1.78, -9.33) * mm});
            skArc(sketch, "E175.0.91", {"start": v(1.78, -9.33) * mm, "mid": v(1.98, -9.3) * mm, "end": v(2.17, -9.25) * mm});
            skLineSegment(sketch, "E175.0.92", {"start": v(2.17, -9.25) * mm, "end": v(2.33, -9) * mm});
            skArc(sketch, "E175.0.93", {"start": v(2.33, -9) * mm, "mid": v(2.87, -8.84) * mm, "end": v(3.4, -8.65) * mm});
            skLineSegment(sketch, "E175.0.94", {"start": v(3.4, -8.65) * mm, "end": v(3.68, -8.76) * mm});
            skArc(sketch, "E175.0.95", {"start": v(3.68, -8.76) * mm, "mid": v(3.86, -8.68) * mm, "end": v(4.05, -8.6) * mm});
            skLineSegment(sketch, "E175.0.96", {"start": v(4.05, -8.6) * mm, "end": v(4.15, -8.32) * mm});
            skArc(sketch, "E175.0.97", {"start": v(4.15, -8.32) * mm, "mid": v(4.65, -8.05) * mm, "end": v(5.13, -7.76) * mm});
            skLineSegment(sketch, "E175.0.98", {"start": v(5.13, -7.76) * mm, "end": v(5.42, -7.8) * mm});
            skArc(sketch, "E175.0.99", {"start": v(5.42, -7.8) * mm, "mid": v(5.58, -7.69) * mm, "end": v(5.74, -7.57) * mm});
            skLineSegment(sketch, "E175.0.100", {"start": v(5.74, -7.57) * mm, "end": v(5.8, -7.28) * mm});
            skArc(sketch, "E175.0.101", {"start": v(5.8, -7.28) * mm, "mid": v(6.22, -6.91) * mm, "end": v(6.63, -6.52) * mm});
            skLineSegment(sketch, "E175.0.102", {"start": v(6.63, -6.52) * mm, "end": v(6.92, -6.5) * mm});
            skArc(sketch, "E175.0.103", {"start": v(6.92, -6.5) * mm, "mid": v(7.06, -6.36) * mm, "end": v(7.2, -6.2) * mm});
            skLineSegment(sketch, "E175.0.104", {"start": v(7.2, -6.2) * mm, "end": v(7.18, -5.91) * mm});
            skArc(sketch, "E175.0.105", {"start": v(7.18, -5.91) * mm, "mid": v(7.52, -5.47) * mm, "end": v(7.84, -5) * mm});
            skLineSegment(sketch, "E175.0.106", {"start": v(7.84, -5) * mm, "end": v(8.13, -4.92) * mm});
            skArc(sketch, "E175.0.107", {"start": v(8.13, -4.92) * mm, "mid": v(8.23, -4.75) * mm, "end": v(8.33, -4.58) * mm});
            skLineSegment(sketch, "E175.0.108", {"start": v(8.33, -4.58) * mm, "end": v(8.25, -4.3) * mm});
            skArc(sketch, "E175.0.109", {"start": v(8.25, -4.3) * mm, "mid": v(8.5, -3.78) * mm, "end": v(8.71, -3.26) * mm});
            skLineSegment(sketch, "E175.0.110", {"start": v(8.71, -3.26) * mm, "end": v(8.97, -3.13) * mm});
            skArc(sketch, "E175.0.111", {"start": v(8.97, -3.13) * mm, "mid": v(9.04, -2.94) * mm, "end": v(9.1, -2.74) * mm});
            skLineSegment(sketch, "E175.0.112", {"start": v(9.1, -2.74) * mm, "end": v(8.96, -2.48) * mm});
            skArc(sketch, "E175.0.113", {"start": v(8.96, -2.48) * mm, "mid": v(9.1, -1.93) * mm, "end": v(9.2, -1.38) * mm});
            skLineSegment(sketch, "E175.0.114", {"start": v(9.2, -1.38) * mm, "end": v(9.42, -1.2) * mm});
            skArc(sketch, "E175.0.115", {"start": v(9.42, -1.2) * mm, "mid": v(9.45, -1) * mm, "end": v(9.47, -0.8) * mm});
            skLineSegment(sketch, "E175.0.116", {"start": v(9.47, -0.8) * mm, "end": v(9.28, -0.57) * mm});
            skArc(sketch, "E175.0.117", {"start": v(9.28, -0.57) * mm, "mid": v(9.3, 0) * mm, "end": v(9.28, 0.57) * mm});
            skLineSegment(sketch, "E175.0.118", {"start": v(9.28, 0.57) * mm, "end": v(9.47, 0.8) * mm});
            skArc(sketch, "E175.0.119", {"start": v(9.47, 0.8) * mm, "mid": v(9.45, 1) * mm, "end": v(9.42, 1.2) * mm});
            skSolve(sketch);
        }
        {
            var Q0;
            Q0=makeQuery(id+"F6.imprint","IMPRINT",FACE,{"disambiguationData":[TD([[makeQuery(id+"F6.imprint","IMPRINT",EDGE,{"derivedFrom":sQuery(id+"F6.wireOp",EDGE,"E175.0.0")}),-1.0]])]});
            extrude(context, id + "F7", {"entities" : qUnion([Q0]), "operationType" : NewBodyOperationType.ADD, "depth" : (getVariable(context, 'Bore_Depth_F')) * mm});
        }
        {
            var Q0;
            Q0=makeQuery(id+"F7.opExtrude","CAP_FACE",FACE,{"disambiguationData":[OSD([sQuery(id+"F6.wireOp",EDGE,"E174"),sQuery(id+"F6.wireOp",EDGE,"E175.0.0"),sQuery(id+"F6.wireOp",EDGE,"E175.0.1"),sQuery(id+"F6.wireOp",EDGE,"E175.0.2"),sQuery(id+"F6.wireOp",EDGE,"E175.0.3"),sQuery(id+"F6.wireOp",EDGE,"E175.0.4"),sQuery(id+"F6.wireOp",EDGE,"E175.0.5"),sQuery(id+"F6.wireOp",EDGE,"E175.0.6"),sQuery(id+"F6.wireOp",EDGE,"E175.0.7"),sQuery(id+"F6.wireOp",EDGE,"E175.0.8"),sQuery(id+"F6.wireOp",EDGE,"E175.0.9"),sQuery(id+"F6.wireOp",EDGE,"E175.0.10"),sQuery(id+"F6.wireOp",EDGE,"E175.0.11"),sQuery(id+"F6.wireOp",EDGE,"E175.0.12"),sQuery(id+"F6.wireOp",EDGE,"E175.0.13"),sQuery(id+"F6.wireOp",EDGE,"E175.0.14"),sQuery(id+"F6.wireOp",EDGE,"E175.0.15"),sQuery(id+"F6.wireOp",EDGE,"E175.0.16"),sQuery(id+"F6.wireOp",EDGE,"E175.0.17"),sQuery(id+"F6.wireOp",EDGE,"E175.0.18"),sQuery(id+"F6.wireOp",EDGE,"E175.0.19"),sQuery(id+"F6.wireOp",EDGE,"E175.0.20"),sQuery(id+"F6.wireOp",EDGE,"E175.0.21"),sQuery(id+"F6.wireOp",EDGE,"E175.0.22"),sQuery(id+"F6.wireOp",EDGE,"E175.0.23"),sQuery(id+"F6.wireOp",EDGE,"E175.0.24"),sQuery(id+"F6.wireOp",EDGE,"E175.0.25"),sQuery(id+"F6.wireOp",EDGE,"E175.0.26"),sQuery(id+"F6.wireOp",EDGE,"E175.0.27"),sQuery(id+"F6.wireOp",EDGE,"E175.0.28"),sQuery(id+"F6.wireOp",EDGE,"E175.0.29"),sQuery(id+"F6.wireOp",EDGE,"E175.0.30"),sQuery(id+"F6.wireOp",EDGE,"E175.0.31"),sQuery(id+"F6.wireOp",EDGE,"E175.0.32"),sQuery(id+"F6.wireOp",EDGE,"E175.0.33"),sQuery(id+"F6.wireOp",EDGE,"E175.0.34"),sQuery(id+"F6.wireOp",EDGE,"E175.0.35"),sQuery(id+"F6.wireOp",EDGE,"E175.0.36"),sQuery(id+"F6.wireOp",EDGE,"E175.0.37"),sQuery(id+"F6.wireOp",EDGE,"E175.0.38"),sQuery(id+"F6.wireOp",EDGE,"E175.0.39"),sQuery(id+"F6.wireOp",EDGE,"E175.0.40"),sQuery(id+"F6.wireOp",EDGE,"E175.0.41"),sQuery(id+"F6.wireOp",EDGE,"E175.0.42"),sQuery(id+"F6.wireOp",EDGE,"E175.0.43"),sQuery(id+"F6.wireOp",EDGE,"E175.0.44"),sQuery(id+"F6.wireOp",EDGE,"E175.0.45"),sQuery(id+"F6.wireOp",EDGE,"E175.0.46"),sQuery(id+"F6.wireOp",EDGE,"E175.0.47"),sQuery(id+"F6.wireOp",EDGE,"E175.0.48"),sQuery(id+"F6.wireOp",EDGE,"E175.0.49"),sQuery(id+"F6.wireOp",EDGE,"E175.0.50"),sQuery(id+"F6.wireOp",EDGE,"E175.0.51"),sQuery(id+"F6.wireOp",EDGE,"E175.0.52"),sQuery(id+"F6.wireOp",EDGE,"E175.0.53"),sQuery(id+"F6.wireOp",EDGE,"E175.0.54"),sQuery(id+"F6.wireOp",EDGE,"E175.0.55"),sQuery(id+"F6.wireOp",EDGE,"E175.0.56"),sQuery(id+"F6.wireOp",EDGE,"E175.0.57"),sQuery(id+"F6.wireOp",EDGE,"E175.0.58"),sQuery(id+"F6.wireOp",EDGE,"E175.0.59"),sQuery(id+"F6.wireOp",EDGE,"E175.0.60"),sQuery(id+"F6.wireOp",EDGE,"E175.0.61"),sQuery(id+"F6.wireOp",EDGE,"E175.0.62"),sQuery(id+"F6.wireOp",EDGE,"E175.0.63"),sQuery(id+"F6.wireOp",EDGE,"E175.0.64"),sQuery(id+"F6.wireOp",EDGE,"E175.0.65"),sQuery(id+"F6.wireOp",EDGE,"E175.0.66"),sQuery(id+"F6.wireOp",EDGE,"E175.0.67"),sQuery(id+"F6.wireOp",EDGE,"E175.0.68"),sQuery(id+"F6.wireOp",EDGE,"E175.0.69"),sQuery(id+"F6.wireOp",EDGE,"E175.0.70"),sQuery(id+"F6.wireOp",EDGE,"E175.0.71"),sQuery(id+"F6.wireOp",EDGE,"E175.0.72"),sQuery(id+"F6.wireOp",EDGE,"E175.0.73"),sQuery(id+"F6.wireOp",EDGE,"E175.0.74"),sQuery(id+"F6.wireOp",EDGE,"E175.0.75"),sQuery(id+"F6.wireOp",EDGE,"E175.0.76"),sQuery(id+"F6.wireOp",EDGE,"E175.0.77"),sQuery(id+"F6.wireOp",EDGE,"E175.0.78"),sQuery(id+"F6.wireOp",EDGE,"E175.0.79"),sQuery(id+"F6.wireOp",EDGE,"E175.0.80"),sQuery(id+"F6.wireOp",EDGE,"E175.0.81"),sQuery(id+"F6.wireOp",EDGE,"E175.0.82"),sQuery(id+"F6.wireOp",EDGE,"E175.0.83"),sQuery(id+"F6.wireOp",EDGE,"E175.0.84"),sQuery(id+"F6.wireOp",EDGE,"E175.0.85"),sQuery(id+"F6.wireOp",EDGE,"E175.0.86"),sQuery(id+"F6.wireOp",EDGE,"E175.0.87"),sQuery(id+"F6.wireOp",EDGE,"E175.0.88"),sQuery(id+"F6.wireOp",EDGE,"E175.0.89"),sQuery(id+"F6.wireOp",EDGE,"E175.0.90"),sQuery(id+"F6.wireOp",EDGE,"E175.0.91"),sQuery(id+"F6.wireOp",EDGE,"E175.0.92"),sQuery(id+"F6.wireOp",EDGE,"E175.0.93"),sQuery(id+"F6.wireOp",EDGE,"E175.0.94"),sQuery(id+"F6.wireOp",EDGE,"E175.0.95"),sQuery(id+"F6.wireOp",EDGE,"E175.0.96"),sQuery(id+"F6.wireOp",EDGE,"E175.0.97"),sQuery(id+"F6.wireOp",EDGE,"E175.0.98"),sQuery(id+"F6.wireOp",EDGE,"E175.0.99"),sQuery(id+"F6.wireOp",EDGE,"E175.0.100"),sQuery(id+"F6.wireOp",EDGE,"E175.0.101"),sQuery(id+"F6.wireOp",EDGE,"E175.0.102"),sQuery(id+"F6.wireOp",EDGE,"E175.0.103"),sQuery(id+"F6.wireOp",EDGE,"E175.0.104"),sQuery(id+"F6.wireOp",EDGE,"E175.0.105"),sQuery(id+"F6.wireOp",EDGE,"E175.0.106"),sQuery(id+"F6.wireOp",EDGE,"E175.0.107"),sQuery(id+"F6.wireOp",EDGE,"E175.0.108"),sQuery(id+"F6.wireOp",EDGE,"E175.0.109"),sQuery(id+"F6.wireOp",EDGE,"E175.0.110"),sQuery(id+"F6.wireOp",EDGE,"E175.0.111"),sQuery(id+"F6.wireOp",EDGE,"E175.0.112"),sQuery(id+"F6.wireOp",EDGE,"E175.0.113"),sQuery(id+"F6.wireOp",EDGE,"E175.0.114"),sQuery(id+"F6.wireOp",EDGE,"E175.0.115"),sQuery(id+"F6.wireOp",EDGE,"E175.0.116"),sQuery(id+"F6.wireOp",EDGE,"E175.0.117"),sQuery(id+"F6.wireOp",EDGE,"E175.0.118"),sQuery(id+"F6.wireOp",EDGE,"E175.0.119")])],"isStart":false});
            var sketch = newSketch(context, id + "F8", { "sketchPlane" : qUnion([Q0])});
            skCircle(sketch, "E176", {"center": v(0, 0) * mm, "radius": 8 * mm});
            skCircle(sketch, "E177", {"center": v(0, 0) * mm, "radius": 9.5 * mm});
            skSolve(sketch);
        }
        {
            var Q0;
            Q0=qSketchRegion(id+"F8",true);
            extrude(context, id + "F9", {"entities" : qUnion([Q0]), "oppositeDirection" : true, "depth" : (getVariable(context, 'Main_Length')) * mm});
        }
        {
            var Q0;
            Q0=makeQuery(id+"F5.opExtrude","CAP_FACE",FACE,{"disambiguationData":[OSD([sQuery(id+"F4.wireOp",EDGE,"E0"),sQuery(id+"F4.wireOp",EDGE,"E1"),sQuery(id+"F4.wireOp",EDGE,"E2"),sQuery(id+"F4.wireOp",EDGE,"E3"),sQuery(id+"F4.wireOp",EDGE,"E4"),sQuery(id+"F4.wireOp",EDGE,"E5"),sQuery(id+"F4.wireOp",EDGE,"E6"),sQuery(id+"F4.wireOp",EDGE,"E7"),sQuery(id+"F4.wireOp",EDGE,"E8"),sQuery(id+"F4.wireOp",EDGE,"E9"),sQuery(id+"F4.wireOp",EDGE,"E10"),sQuery(id+"F4.wireOp",EDGE,"E11"),sQuery(id+"F4.wireOp",EDGE,"E12"),sQuery(id+"F4.wireOp",EDGE,"E13"),sQuery(id+"F4.wireOp",EDGE,"E14"),sQuery(id+"F4.wireOp",EDGE,"E15"),sQuery(id+"F4.wireOp",EDGE,"E16"),sQuery(id+"F4.wireOp",EDGE,"E17"),sQuery(id+"F4.wireOp",EDGE,"E18"),sQuery(id+"F4.wireOp",EDGE,"E19"),sQuery(id+"F4.wireOp",EDGE,"E20"),sQuery(id+"F4.wireOp",EDGE,"E21"),sQuery(id+"F4.wireOp",EDGE,"E22"),sQuery(id+"F4.wireOp",EDGE,"E23"),sQuery(id+"F4.wireOp",EDGE,"E24"),sQuery(id+"F4.wireOp",EDGE,"E25"),sQuery(id+"F4.wireOp",EDGE,"E26"),sQuery(id+"F4.wireOp",EDGE,"E27"),sQuery(id+"F4.wireOp",EDGE,"E28"),sQuery(id+"F4.wireOp",EDGE,"E29"),sQuery(id+"F4.wireOp",EDGE,"E30"),sQuery(id+"F4.wireOp",EDGE,"E31"),sQuery(id+"F4.wireOp",EDGE,"E32"),sQuery(id+"F4.wireOp",EDGE,"E33"),sQuery(id+"F4.wireOp",EDGE,"E34"),sQuery(id+"F4.wireOp",EDGE,"E35"),sQuery(id+"F4.wireOp",EDGE,"E36"),sQuery(id+"F4.wireOp",EDGE,"E37"),sQuery(id+"F4.wireOp",EDGE,"E38"),sQuery(id+"F4.wireOp",EDGE,"E39"),sQuery(id+"F4.wireOp",EDGE,"E40"),sQuery(id+"F4.wireOp",EDGE,"E41"),sQuery(id+"F4.wireOp",EDGE,"E42"),sQuery(id+"F4.wireOp",EDGE,"E43"),sQuery(id+"F4.wireOp",EDGE,"E44"),sQuery(id+"F4.wireOp",EDGE,"E45"),sQuery(id+"F4.wireOp",EDGE,"E46"),sQuery(id+"F4.wireOp",EDGE,"E47"),sQuery(id+"F4.wireOp",EDGE,"E48"),sQuery(id+"F4.wireOp",EDGE,"E49"),sQuery(id+"F4.wireOp",EDGE,"E50"),sQuery(id+"F4.wireOp",EDGE,"E51"),sQuery(id+"F4.wireOp",EDGE,"E52"),sQuery(id+"F4.wireOp",EDGE,"E53"),sQuery(id+"F4.wireOp",EDGE,"E54"),sQuery(id+"F4.wireOp",EDGE,"E55"),sQuery(id+"F4.wireOp",EDGE,"E56"),sQuery(id+"F4.wireOp",EDGE,"E57"),sQuery(id+"F4.wireOp",EDGE,"E58"),sQuery(id+"F4.wireOp",EDGE,"E59"),sQuery(id+"F4.wireOp",EDGE,"E60"),sQuery(id+"F4.wireOp",EDGE,"E61"),sQuery(id+"F4.wireOp",EDGE,"E62"),sQuery(id+"F4.wireOp",EDGE,"E63"),sQuery(id+"F4.wireOp",EDGE,"E64"),sQuery(id+"F4.wireOp",EDGE,"E65"),sQuery(id+"F4.wireOp",EDGE,"E66"),sQuery(id+"F4.wireOp",EDGE,"E67"),sQuery(id+"F4.wireOp",EDGE,"E68"),sQuery(id+"F4.wireOp",EDGE,"E69"),sQuery(id+"F4.wireOp",EDGE,"E70"),sQuery(id+"F4.wireOp",EDGE,"E71"),sQuery(id+"F4.wireOp",EDGE,"E72"),sQuery(id+"F4.wireOp",EDGE,"E73"),sQuery(id+"F4.wireOp",EDGE,"E74"),sQuery(id+"F4.wireOp",EDGE,"E75"),sQuery(id+"F4.wireOp",EDGE,"E76"),sQuery(id+"F4.wireOp",EDGE,"E77"),sQuery(id+"F4.wireOp",EDGE,"E78"),sQuery(id+"F4.wireOp",EDGE,"E79"),sQuery(id+"F4.wireOp",EDGE,"E80"),sQuery(id+"F4.wireOp",EDGE,"E81"),sQuery(id+"F4.wireOp",EDGE,"E82"),sQuery(id+"F4.wireOp",EDGE,"E83"),sQuery(id+"F4.wireOp",EDGE,"E84"),sQuery(id+"F4.wireOp",EDGE,"E85"),sQuery(id+"F4.wireOp",EDGE,"E86"),sQuery(id+"F4.wireOp",EDGE,"E87"),sQuery(id+"F4.wireOp",EDGE,"E88"),sQuery(id+"F4.wireOp",EDGE,"E89"),sQuery(id+"F4.wireOp",EDGE,"E90"),sQuery(id+"F4.wireOp",EDGE,"E91"),sQuery(id+"F4.wireOp",EDGE,"E92"),sQuery(id+"F4.wireOp",EDGE,"E93"),sQuery(id+"F4.wireOp",EDGE,"E94"),sQuery(id+"F4.wireOp",EDGE,"E95"),sQuery(id+"F4.wireOp",EDGE,"E96"),sQuery(id+"F4.wireOp",EDGE,"E97"),sQuery(id+"F4.wireOp",EDGE,"E98"),sQuery(id+"F4.wireOp",EDGE,"E99"),sQuery(id+"F4.wireOp",EDGE,"E100"),sQuery(id+"F4.wireOp",EDGE,"E101"),sQuery(id+"F4.wireOp",EDGE,"E102"),sQuery(id+"F4.wireOp",EDGE,"E103"),sQuery(id+"F4.wireOp",EDGE,"E104"),sQuery(id+"F4.wireOp",EDGE,"E105"),sQuery(id+"F4.wireOp",EDGE,"E106"),sQuery(id+"F4.wireOp",EDGE,"E107"),sQuery(id+"F4.wireOp",EDGE,"E108"),sQuery(id+"F4.wireOp",EDGE,"E109"),sQuery(id+"F4.wireOp",EDGE,"E110"),sQuery(id+"F4.wireOp",EDGE,"E111"),sQuery(id+"F4.wireOp",EDGE,"E112"),sQuery(id+"F4.wireOp",EDGE,"E113"),sQuery(id+"F4.wireOp",EDGE,"E114"),sQuery(id+"F4.wireOp",EDGE,"E115"),sQuery(id+"F4.wireOp",EDGE,"E116"),sQuery(id+"F4.wireOp",EDGE,"E117"),sQuery(id+"F4.wireOp",EDGE,"E118"),sQuery(id+"F4.wireOp",EDGE,"E119"),sQuery(id+"F4.wireOp",EDGE,"E120"),sQuery(id+"F4.wireOp",EDGE,"E121"),sQuery(id+"F4.wireOp",EDGE,"E122"),sQuery(id+"F4.wireOp",EDGE,"E123"),sQuery(id+"F4.wireOp",EDGE,"E124"),sQuery(id+"F4.wireOp",EDGE,"E125"),sQuery(id+"F4.wireOp",EDGE,"E126"),sQuery(id+"F4.wireOp",EDGE,"E127"),sQuery(id+"F4.wireOp",EDGE,"E128"),sQuery(id+"F4.wireOp",EDGE,"E129"),sQuery(id+"F4.wireOp",EDGE,"E130"),sQuery(id+"F4.wireOp",EDGE,"E131"),sQuery(id+"F4.wireOp",EDGE,"E132"),sQuery(id+"F4.wireOp",EDGE,"E133"),sQuery(id+"F4.wireOp",EDGE,"E134"),sQuery(id+"F4.wireOp",EDGE,"E135"),sQuery(id+"F4.wireOp",EDGE,"E136"),sQuery(id+"F4.wireOp",EDGE,"E137"),sQuery(id+"F4.wireOp",EDGE,"E138"),sQuery(id+"F4.wireOp",EDGE,"E139"),sQuery(id+"F4.wireOp",EDGE,"E140"),sQuery(id+"F4.wireOp",EDGE,"E141"),sQuery(id+"F4.wireOp",EDGE,"E142"),sQuery(id+"F4.wireOp",EDGE,"E143"),sQuery(id+"F4.wireOp",EDGE,"E144"),sQuery(id+"F4.wireOp",EDGE,"E145"),sQuery(id+"F4.wireOp",EDGE,"E146"),sQuery(id+"F4.wireOp",EDGE,"E147"),sQuery(id+"F4.wireOp",EDGE,"E148"),sQuery(id+"F4.wireOp",EDGE,"E149"),sQuery(id+"F4.wireOp",EDGE,"E150"),sQuery(id+"F4.wireOp",EDGE,"E151"),sQuery(id+"F4.wireOp",EDGE,"E152"),sQuery(id+"F4.wireOp",EDGE,"E153"),sQuery(id+"F4.wireOp",EDGE,"E154"),sQuery(id+"F4.wireOp",EDGE,"E155"),sQuery(id+"F4.wireOp",EDGE,"E156"),sQuery(id+"F4.wireOp",EDGE,"E157"),sQuery(id+"F4.wireOp",EDGE,"E158"),sQuery(id+"F4.wireOp",EDGE,"E159"),sQuery(id+"F4.wireOp",EDGE,"E160"),sQuery(id+"F4.wireOp",EDGE,"E161"),sQuery(id+"F4.wireOp",EDGE,"E162"),sQuery(id+"F4.wireOp",EDGE,"E163"),sQuery(id+"F4.wireOp",EDGE,"E164"),sQuery(id+"F4.wireOp",EDGE,"E165"),sQuery(id+"F4.wireOp",EDGE,"E166"),sQuery(id+"F4.wireOp",EDGE,"E167"),sQuery(id+"F4.wireOp",EDGE,"E168"),sQuery(id+"F4.wireOp",EDGE,"E169"),sQuery(id+"F4.wireOp",EDGE,"E170"),sQuery(id+"F4.wireOp",EDGE,"E171"),sQuery(id+"F4.wireOp",EDGE,"E172"),sQuery(id+"F4.wireOp",EDGE,"E173")])],"isStart":true});
            var sketch = newSketch(context, id + "F10", { "sketchPlane" : qUnion([Q0])});
            skCircle(sketch, "E178", {"center": v(0, 0) * mm, "radius": 8 * mm});
            skLineSegment(sketch, "E179.0.0", {"start": v(-9.2, 1.38) * mm, "end": v(-9.42, 1.2) * mm});
            skArc(sketch, "E179.0.1", {"start": v(-9.42, 1.2) * mm, "mid": v(-9.45, 1) * mm, "end": v(-9.47, 0.8) * mm});
            skLineSegment(sketch, "E179.0.2", {"start": v(-9.47, 0.8) * mm, "end": v(-9.28, 0.57) * mm});
            skArc(sketch, "E179.0.3", {"start": v(-9.28, 0.57) * mm, "mid": v(-9.3, 0) * mm, "end": v(-9.28, -0.57) * mm});
            skLineSegment(sketch, "E179.0.4", {"start": v(-9.28, -0.57) * mm, "end": v(-9.47, -0.8) * mm});
            skArc(sketch, "E179.0.5", {"start": v(-9.47, -0.8) * mm, "mid": v(-9.45, -1) * mm, "end": v(-9.42, -1.2) * mm});
            skLineSegment(sketch, "E179.0.6", {"start": v(-9.42, -1.2) * mm, "end": v(-9.2, -1.38) * mm});
            skArc(sketch, "E179.0.7", {"start": v(-9.2, -1.38) * mm, "mid": v(-9.1, -1.93) * mm, "end": v(-8.96, -2.48) * mm});
            skLineSegment(sketch, "E179.0.8", {"start": v(-8.96, -2.48) * mm, "end": v(-9.1, -2.74) * mm});
            skArc(sketch, "E179.0.9", {"start": v(-9.1, -2.74) * mm, "mid": v(-9.04, -2.94) * mm, "end": v(-8.97, -3.13) * mm});
            skLineSegment(sketch, "E179.0.10", {"start": v(-8.97, -3.13) * mm, "end": v(-8.71, -3.26) * mm});
            skArc(sketch, "E179.0.11", {"start": v(-8.71, -3.26) * mm, "mid": v(-8.5, -3.78) * mm, "end": v(-8.25, -4.3) * mm});
            skLineSegment(sketch, "E179.0.12", {"start": v(-8.25, -4.3) * mm, "end": v(-8.33, -4.58) * mm});
            skArc(sketch, "E179.0.13", {"start": v(-8.33, -4.58) * mm, "mid": v(-8.23, -4.75) * mm, "end": v(-8.13, -4.92) * mm});
            skLineSegment(sketch, "E179.0.14", {"start": v(-8.13, -4.92) * mm, "end": v(-7.84, -5) * mm});
            skArc(sketch, "E179.0.15", {"start": v(-7.84, -5) * mm, "mid": v(-7.52, -5.47) * mm, "end": v(-7.18, -5.91) * mm});
            skLineSegment(sketch, "E179.0.16", {"start": v(-7.18, -5.91) * mm, "end": v(-7.2, -6.2) * mm});
            skArc(sketch, "E179.0.17", {"start": v(-7.2, -6.2) * mm, "mid": v(-7.06, -6.36) * mm, "end": v(-6.92, -6.5) * mm});
            skLineSegment(sketch, "E179.0.18", {"start": v(-6.92, -6.5) * mm, "end": v(-6.63, -6.52) * mm});
            skArc(sketch, "E179.0.19", {"start": v(-6.63, -6.52) * mm, "mid": v(-6.22, -6.91) * mm, "end": v(-5.8, -7.28) * mm});
            skLineSegment(sketch, "E179.0.20", {"start": v(-5.8, -7.28) * mm, "end": v(-5.74, -7.57) * mm});
            skArc(sketch, "E179.0.21", {"start": v(-5.74, -7.57) * mm, "mid": v(-5.58, -7.69) * mm, "end": v(-5.42, -7.8) * mm});
            skLineSegment(sketch, "E179.0.22", {"start": v(-5.42, -7.8) * mm, "end": v(-5.13, -7.76) * mm});
            skArc(sketch, "E179.0.23", {"start": v(-5.13, -7.76) * mm, "mid": v(-4.65, -8.05) * mm, "end": v(-4.15, -8.32) * mm});
            skLineSegment(sketch, "E179.0.24", {"start": v(-4.15, -8.32) * mm, "end": v(-4.05, -8.6) * mm});
            skArc(sketch, "E179.0.25", {"start": v(-4.05, -8.6) * mm, "mid": v(-3.86, -8.68) * mm, "end": v(-3.68, -8.76) * mm});
            skLineSegment(sketch, "E179.0.26", {"start": v(-3.68, -8.76) * mm, "end": v(-3.4, -8.65) * mm});
            skArc(sketch, "E179.0.27", {"start": v(-3.4, -8.65) * mm, "mid": v(-2.87, -8.84) * mm, "end": v(-2.33, -9) * mm});
            skLineSegment(sketch, "E179.0.28", {"start": v(-2.33, -9) * mm, "end": v(-2.17, -9.25) * mm});
            skArc(sketch, "E179.0.29", {"start": v(-2.17, -9.25) * mm, "mid": v(-1.98, -9.3) * mm, "end": v(-1.78, -9.33) * mm});
            skLineSegment(sketch, "E179.0.30", {"start": v(-1.78, -9.33) * mm, "end": v(-1.53, -9.17) * mm});
            skArc(sketch, "E179.0.31", {"start": v(-1.53, -9.17) * mm, "mid": v(-0.97, -9.25) * mm, "end": v(-0.4, -9.3) * mm});
            skLineSegment(sketch, "E179.0.32", {"start": v(-0.4, -9.3) * mm, "end": v(-0.2, -9.5) * mm});
            skArc(sketch, "E179.0.33", {"start": v(-0.2, -9.5) * mm, "mid": v(0, -9.5) * mm, "end": v(0.2, -9.5) * mm});
            skLineSegment(sketch, "E179.0.34", {"start": v(0.2, -9.5) * mm, "end": v(0.4, -9.3) * mm});
            skArc(sketch, "E179.0.35", {"start": v(0.4, -9.3) * mm, "mid": v(0.97, -9.25) * mm, "end": v(1.53, -9.17) * mm});
            skLineSegment(sketch, "E179.0.36", {"start": v(1.53, -9.17) * mm, "end": v(1.78, -9.33) * mm});
            skArc(sketch, "E179.0.37", {"start": v(1.78, -9.33) * mm, "mid": v(1.98, -9.3) * mm, "end": v(2.17, -9.25) * mm});
            skLineSegment(sketch, "E179.0.38", {"start": v(2.17, -9.25) * mm, "end": v(2.33, -9) * mm});
            skArc(sketch, "E179.0.39", {"start": v(2.33, -9) * mm, "mid": v(2.87, -8.84) * mm, "end": v(3.4, -8.65) * mm});
            skLineSegment(sketch, "E179.0.40", {"start": v(3.4, -8.65) * mm, "end": v(3.68, -8.76) * mm});
            skArc(sketch, "E179.0.41", {"start": v(3.68, -8.76) * mm, "mid": v(3.86, -8.68) * mm, "end": v(4.05, -8.6) * mm});
            skLineSegment(sketch, "E179.0.42", {"start": v(4.05, -8.6) * mm, "end": v(4.15, -8.32) * mm});
            skArc(sketch, "E179.0.43", {"start": v(4.15, -8.32) * mm, "mid": v(4.65, -8.05) * mm, "end": v(5.13, -7.76) * mm});
            skLineSegment(sketch, "E179.0.44", {"start": v(5.13, -7.76) * mm, "end": v(5.42, -7.8) * mm});
            skArc(sketch, "E179.0.45", {"start": v(5.42, -7.8) * mm, "mid": v(5.58, -7.69) * mm, "end": v(5.74, -7.57) * mm});
            skLineSegment(sketch, "E179.0.46", {"start": v(5.74, -7.57) * mm, "end": v(5.8, -7.28) * mm});
            skArc(sketch, "E179.0.47", {"start": v(5.8, -7.28) * mm, "mid": v(6.22, -6.91) * mm, "end": v(6.63, -6.52) * mm});
            skLineSegment(sketch, "E179.0.48", {"start": v(6.63, -6.52) * mm, "end": v(6.92, -6.5) * mm});
            skArc(sketch, "E179.0.49", {"start": v(6.92, -6.5) * mm, "mid": v(7.06, -6.36) * mm, "end": v(7.2, -6.2) * mm});
            skLineSegment(sketch, "E179.0.50", {"start": v(7.2, -6.2) * mm, "end": v(7.18, -5.91) * mm});
            skArc(sketch, "E179.0.51", {"start": v(7.18, -5.91) * mm, "mid": v(7.52, -5.47) * mm, "end": v(7.84, -5) * mm});
            skLineSegment(sketch, "E179.0.52", {"start": v(7.84, -5) * mm, "end": v(8.13, -4.92) * mm});
            skArc(sketch, "E179.0.53", {"start": v(8.13, -4.92) * mm, "mid": v(8.23, -4.75) * mm, "end": v(8.33, -4.58) * mm});
            skLineSegment(sketch, "E179.0.54", {"start": v(8.33, -4.58) * mm, "end": v(8.25, -4.3) * mm});
            skArc(sketch, "E179.0.55", {"start": v(8.25, -4.3) * mm, "mid": v(8.5, -3.78) * mm, "end": v(8.71, -3.26) * mm});
            skLineSegment(sketch, "E179.0.56", {"start": v(8.71, -3.26) * mm, "end": v(8.97, -3.13) * mm});
            skArc(sketch, "E179.0.57", {"start": v(8.97, -3.13) * mm, "mid": v(9.04, -2.94) * mm, "end": v(9.1, -2.74) * mm});
            skLineSegment(sketch, "E179.0.58", {"start": v(9.1, -2.74) * mm, "end": v(8.96, -2.48) * mm});
            skArc(sketch, "E179.0.59", {"start": v(8.96, -2.48) * mm, "mid": v(9.1, -1.93) * mm, "end": v(9.2, -1.38) * mm});
            skLineSegment(sketch, "E179.0.60", {"start": v(9.2, -1.38) * mm, "end": v(9.42, -1.2) * mm});
            skArc(sketch, "E179.0.61", {"start": v(9.42, -1.2) * mm, "mid": v(9.45, -1) * mm, "end": v(9.47, -0.8) * mm});
            skLineSegment(sketch, "E179.0.62", {"start": v(9.47, -0.8) * mm, "end": v(9.28, -0.57) * mm});
            skArc(sketch, "E179.0.63", {"start": v(9.28, -0.57) * mm, "mid": v(9.3, 0) * mm, "end": v(9.28, 0.57) * mm});
            skLineSegment(sketch, "E179.0.64", {"start": v(9.28, 0.57) * mm, "end": v(9.47, 0.8) * mm});
            skArc(sketch, "E179.0.65", {"start": v(9.47, 0.8) * mm, "mid": v(9.45, 1) * mm, "end": v(9.42, 1.2) * mm});
            skLineSegment(sketch, "E179.0.66", {"start": v(9.42, 1.2) * mm, "end": v(9.2, 1.38) * mm});
            skArc(sketch, "E179.0.67", {"start": v(9.2, 1.38) * mm, "mid": v(9.1, 1.93) * mm, "end": v(8.96, 2.48) * mm});
            skLineSegment(sketch, "E179.0.68", {"start": v(8.96, 2.48) * mm, "end": v(9.1, 2.74) * mm});
            skArc(sketch, "E179.0.69", {"start": v(9.1, 2.74) * mm, "mid": v(9.04, 2.94) * mm, "end": v(8.97, 3.13) * mm});
            skLineSegment(sketch, "E179.0.70", {"start": v(8.97, 3.13) * mm, "end": v(8.71, 3.26) * mm});
            skArc(sketch, "E179.0.71", {"start": v(8.71, 3.26) * mm, "mid": v(8.5, 3.78) * mm, "end": v(8.25, 4.3) * mm});
            skLineSegment(sketch, "E179.0.72", {"start": v(8.25, 4.3) * mm, "end": v(8.33, 4.58) * mm});
            skArc(sketch, "E179.0.73", {"start": v(8.33, 4.58) * mm, "mid": v(8.23, 4.75) * mm, "end": v(8.13, 4.92) * mm});
            skLineSegment(sketch, "E179.0.74", {"start": v(8.13, 4.92) * mm, "end": v(7.84, 5) * mm});
            skArc(sketch, "E179.0.75", {"start": v(7.84, 5) * mm, "mid": v(7.52, 5.47) * mm, "end": v(7.18, 5.91) * mm});
            skLineSegment(sketch, "E179.0.76", {"start": v(7.18, 5.91) * mm, "end": v(7.2, 6.2) * mm});
            skArc(sketch, "E179.0.77", {"start": v(7.2, 6.2) * mm, "mid": v(7.06, 6.36) * mm, "end": v(6.92, 6.5) * mm});
            skLineSegment(sketch, "E179.0.78", {"start": v(6.92, 6.5) * mm, "end": v(6.63, 6.52) * mm});
            skArc(sketch, "E179.0.79", {"start": v(6.63, 6.52) * mm, "mid": v(6.22, 6.91) * mm, "end": v(5.8, 7.28) * mm});
            skLineSegment(sketch, "E179.0.80", {"start": v(5.8, 7.28) * mm, "end": v(5.74, 7.57) * mm});
            skArc(sketch, "E179.0.81", {"start": v(5.74, 7.57) * mm, "mid": v(5.58, 7.69) * mm, "end": v(5.42, 7.8) * mm});
            skLineSegment(sketch, "E179.0.82", {"start": v(5.42, 7.8) * mm, "end": v(5.13, 7.76) * mm});
            skArc(sketch, "E179.0.83", {"start": v(5.13, 7.76) * mm, "mid": v(4.65, 8.05) * mm, "end": v(4.15, 8.32) * mm});
            skLineSegment(sketch, "E179.0.84", {"start": v(4.15, 8.32) * mm, "end": v(4.05, 8.6) * mm});
            skArc(sketch, "E179.0.85", {"start": v(4.05, 8.6) * mm, "mid": v(3.86, 8.68) * mm, "end": v(3.68, 8.76) * mm});
            skLineSegment(sketch, "E179.0.86", {"start": v(3.68, 8.76) * mm, "end": v(3.4, 8.65) * mm});
            skArc(sketch, "E179.0.87", {"start": v(3.4, 8.65) * mm, "mid": v(2.87, 8.84) * mm, "end": v(2.33, 9) * mm});
            skLineSegment(sketch, "E179.0.88", {"start": v(2.33, 9) * mm, "end": v(2.17, 9.25) * mm});
            skArc(sketch, "E179.0.89", {"start": v(2.17, 9.25) * mm, "mid": v(1.98, 9.3) * mm, "end": v(1.78, 9.33) * mm});
            skLineSegment(sketch, "E179.0.90", {"start": v(1.78, 9.33) * mm, "end": v(1.53, 9.17) * mm});
            skArc(sketch, "E179.0.91", {"start": v(1.53, 9.17) * mm, "mid": v(0.97, 9.25) * mm, "end": v(0.4, 9.3) * mm});
            skLineSegment(sketch, "E179.0.92", {"start": v(0.4, 9.3) * mm, "end": v(0.2, 9.5) * mm});
            skArc(sketch, "E179.0.93", {"start": v(0.2, 9.5) * mm, "mid": v(0, 9.5) * mm, "end": v(-0.2, 9.5) * mm});
            skLineSegment(sketch, "E179.0.94", {"start": v(-0.2, 9.5) * mm, "end": v(-0.4, 9.3) * mm});
            skArc(sketch, "E179.0.95", {"start": v(-0.4, 9.3) * mm, "mid": v(-0.97, 9.25) * mm, "end": v(-1.53, 9.17) * mm});
            skLineSegment(sketch, "E179.0.96", {"start": v(-1.53, 9.17) * mm, "end": v(-1.78, 9.33) * mm});
            skArc(sketch, "E179.0.97", {"start": v(-1.78, 9.33) * mm, "mid": v(-1.98, 9.3) * mm, "end": v(-2.17, 9.25) * mm});
            skLineSegment(sketch, "E179.0.98", {"start": v(-2.17, 9.25) * mm, "end": v(-2.33, 9) * mm});
            skArc(sketch, "E179.0.99", {"start": v(-2.33, 9) * mm, "mid": v(-2.87, 8.84) * mm, "end": v(-3.4, 8.65) * mm});
            skLineSegment(sketch, "E179.0.100", {"start": v(-3.4, 8.65) * mm, "end": v(-3.68, 8.76) * mm});
            skArc(sketch, "E179.0.101", {"start": v(-3.68, 8.76) * mm, "mid": v(-3.86, 8.68) * mm, "end": v(-4.05, 8.6) * mm});
            skLineSegment(sketch, "E179.0.102", {"start": v(-4.05, 8.6) * mm, "end": v(-4.15, 8.32) * mm});
            skArc(sketch, "E179.0.103", {"start": v(-4.15, 8.32) * mm, "mid": v(-4.65, 8.05) * mm, "end": v(-5.13, 7.76) * mm});
            skLineSegment(sketch, "E179.0.104", {"start": v(-5.13, 7.76) * mm, "end": v(-5.42, 7.8) * mm});
            skArc(sketch, "E179.0.105", {"start": v(-5.42, 7.8) * mm, "mid": v(-5.58, 7.69) * mm, "end": v(-5.74, 7.57) * mm});
            skLineSegment(sketch, "E179.0.106", {"start": v(-5.74, 7.57) * mm, "end": v(-5.8, 7.28) * mm});
            skArc(sketch, "E179.0.107", {"start": v(-5.8, 7.28) * mm, "mid": v(-6.22, 6.91) * mm, "end": v(-6.63, 6.52) * mm});
            skLineSegment(sketch, "E179.0.108", {"start": v(-6.63, 6.52) * mm, "end": v(-6.92, 6.5) * mm});
            skArc(sketch, "E179.0.109", {"start": v(-6.92, 6.5) * mm, "mid": v(-7.06, 6.36) * mm, "end": v(-7.2, 6.2) * mm});
            skLineSegment(sketch, "E179.0.110", {"start": v(-7.2, 6.2) * mm, "end": v(-7.18, 5.91) * mm});
            skArc(sketch, "E179.0.111", {"start": v(-7.18, 5.91) * mm, "mid": v(-7.52, 5.47) * mm, "end": v(-7.84, 5) * mm});
            skLineSegment(sketch, "E179.0.112", {"start": v(-7.84, 5) * mm, "end": v(-8.13, 4.92) * mm});
            skArc(sketch, "E179.0.113", {"start": v(-8.13, 4.92) * mm, "mid": v(-8.23, 4.75) * mm, "end": v(-8.33, 4.58) * mm});
            skLineSegment(sketch, "E179.0.114", {"start": v(-8.33, 4.58) * mm, "end": v(-8.25, 4.3) * mm});
            skArc(sketch, "E179.0.115", {"start": v(-8.25, 4.3) * mm, "mid": v(-8.5, 3.78) * mm, "end": v(-8.71, 3.26) * mm});
            skLineSegment(sketch, "E179.0.116", {"start": v(-8.71, 3.26) * mm, "end": v(-8.97, 3.13) * mm});
            skArc(sketch, "E179.0.117", {"start": v(-8.97, 3.13) * mm, "mid": v(-9.04, 2.94) * mm, "end": v(-9.1, 2.74) * mm});
            skLineSegment(sketch, "E179.0.118", {"start": v(-9.1, 2.74) * mm, "end": v(-8.96, 2.48) * mm});
            skArc(sketch, "E179.0.119", {"start": v(-8.96, 2.48) * mm, "mid": v(-9.1, 1.93) * mm, "end": v(-9.2, 1.38) * mm});
            skSolve(sketch);
        }
        {
            var Q0;
            Q0=makeQuery(id+"F10.imprint","IMPRINT",FACE,{"disambiguationData":[TD([[makeQuery(id+"F10.imprint","IMPRINT",EDGE,{"derivedFrom":sQuery(id+"F10.wireOp",EDGE,"E179.0.0")}),1.0]])]});
            extrude(context, id + "F11", {"entities" : qUnion([Q0]), "operationType" : NewBodyOperationType.ADD, "depth" : (getVariable(context, 'Bore_Depth_R')) * mm});
        }
        {
            var Q0;
            Q0=qCreatedBy(makeId("Right.planeOp"),FACE);
            cPlane(context, id + "F12", {"entities" : qUnion([Q0]), "cplaneType" : CPlaneType.OFFSET, "offset" : (getVariable(context, 'Main_Diam')) / 2 * mm, "oppositeDirection" : true, "width" : 150 * mm, "height" : 150 * mm});
        }
        {
            var Q0;
            Q0=qCreatedBy(id+"F12.planeOp",FACE);
            var sketch = newSketch(context, id + "F13", { "sketchPlane" : qUnion([Q0])});
            skCircle(sketch, "E180", {"center": v(-132, 0) * mm, "radius": 1.25 * mm});
            skPoint(sketch, "E181", {"position": v(-56.13, 0) * mm});
            skCircle(sketch, "E182", {"center": v(-123, 0) * mm, "radius": 3.25 * mm});
            skSolve(sketch);
        }
        {
            var Q0;
            Q0=makeQuery(id+"F13.imprint","IMPRINT",FACE,{"disambiguationData":[TD([[makeQuery(id+"F13.imprint","IMPRINT",EDGE,{"derivedFrom":sQuery(id+"F13.wireOp",EDGE,"E180")}),1.0]])]});
            var Q1;
            Q1=makeQuery(id+"F13.imprint","IMPRINT",FACE,{"disambiguationData":[TD([[makeQuery(id+"F13.imprint","IMPRINT",EDGE,{"derivedFrom":sQuery(id+"F13.wireOp",EDGE,"E182")}),1.0]])]});
            extrude(context, id + "F14", {"entities" : qUnion([Q0, Q1]), "operationType" : NewBodyOperationType.REMOVE, "depth" : 5 * mm});
        }
    });
